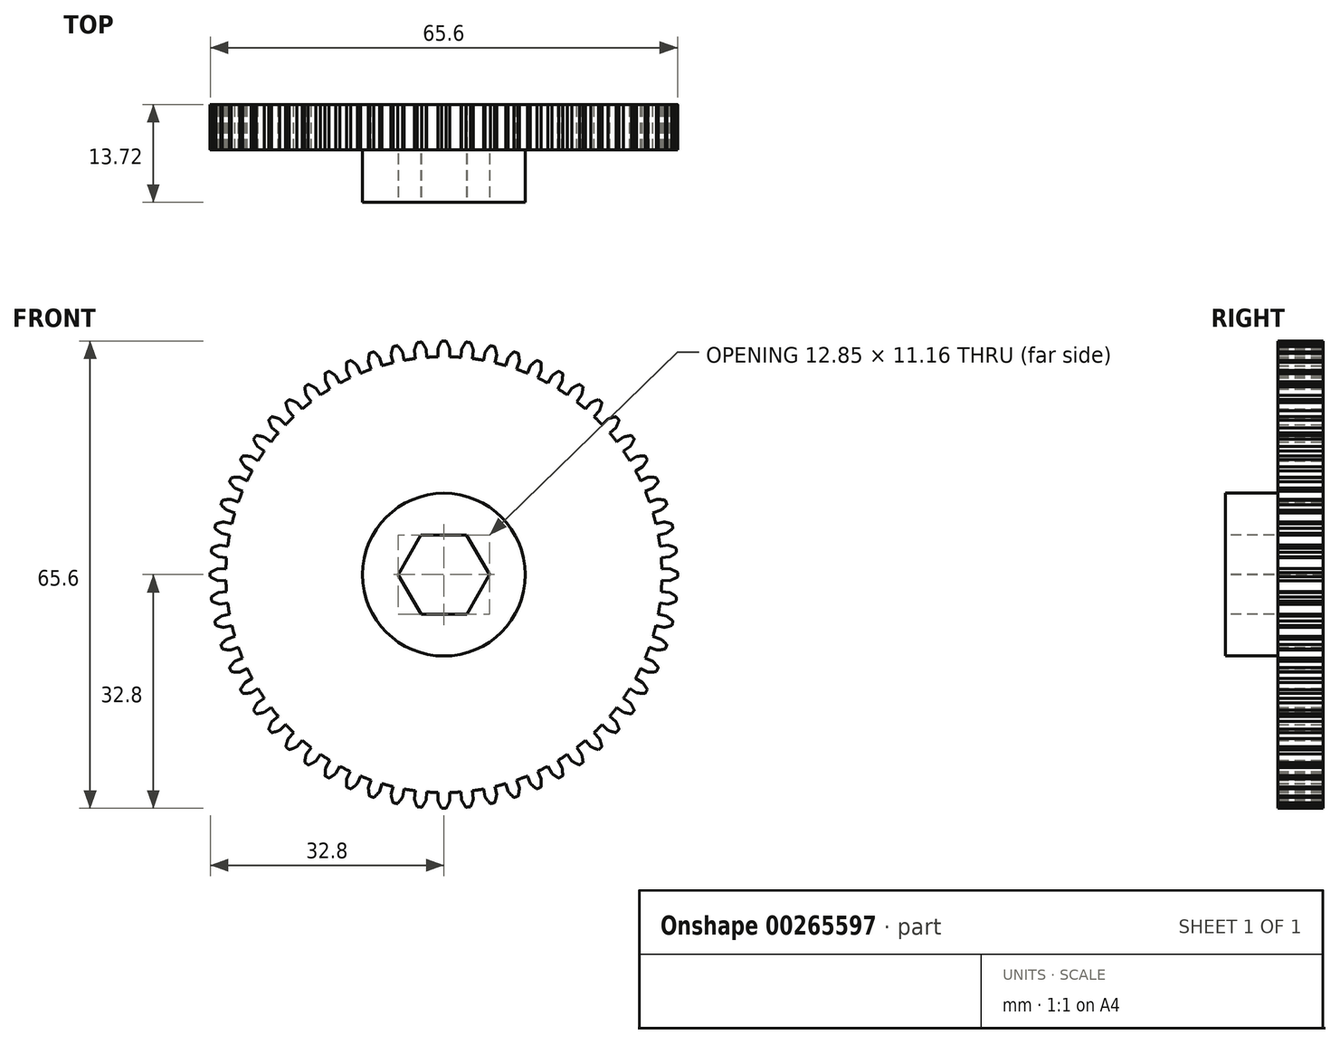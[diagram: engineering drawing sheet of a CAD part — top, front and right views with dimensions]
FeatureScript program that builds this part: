
annotation { "Feature Type Name" : "Feature", "Feature Type Description" : "" }
export const myFeature = defineFeature(function(context is Context, id is Id, definition is map)
    precondition{}
    {
        {
            var Q0;
            Q0=qCreatedBy(makeId("Front.planeOp"),FACE);
            var sketch = newSketch(context, id + "F0", { "sketchPlane" : qUnion([Q0])});
            skCircle(sketch, "E0", {"center": v(0, 0) * mm, "radius": 30.6 * mm});
            skArc(sketch, "E1", {"start": v(0.31, 32.8) * mm, "mid": v(0.16, 32.8) * mm, "end": v(0, 32.8) * mm});
            skLineSegment(sketch, "E2", {"start": v(0.8, 30.6) * mm, "end": v(0.83, 31.74) * mm});
            skLineSegment(sketch, "E3.trimOffspring", {"start": v(-1.66, 31.7) * mm, "end": v(-1.66, 31.74) * mm});
            skArc(sketch, "E4.trimOffspring", {"start": v(0.83, 31.74) * mm, "mid": v(0.6, 32.28) * mm, "end": v(0.31, 32.8) * mm});
            skLineSegment(sketch, "E5", {"start": v(0, 0) * mm, "end": v(0, 44.4) * mm, "construction": true});
            skArc(sketch, "E6.MirrorCS", {"start": v(-0.83, 31.74) * mm, "mid": v(-0.6, 32.28) * mm, "end": v(-0.31, 32.8) * mm});
            skPoint(sketch, "E7.orphan", {"position": v(-1.15, 44.01) * mm});
            skPoint(sketch, "E8.orphan", {"position": v(1.15, 44.01) * mm});
            skLineSegment(sketch, "E9.MirrorCS", {"start": v(-0.8, 30.6) * mm, "end": v(-0.83, 31.74) * mm});
            skArc(sketch, "E10.MirrorCS", {"start": v(-0.31, 32.8) * mm, "mid": v(-0.16, 32.8) * mm, "end": v(0, 32.8) * mm});
            skArc(sketch, "E11.1.0", {"start": v(-2.5, 31.65) * mm, "mid": v(-2.79, 32.17) * mm, "end": v(-3.12, 32.66) * mm});
            skLineSegment(sketch, "E11.1.1", {"start": v(-4, 30.35) * mm, "end": v(-4.14, 31.48) * mm});
            skLineSegment(sketch, "E11.1.2", {"start": v(-2.4, 30.51) * mm, "end": v(-2.5, 31.65) * mm});
            skArc(sketch, "E11.1.3", {"start": v(-4.14, 31.48) * mm, "mid": v(-3.96, 32.04) * mm, "end": v(-3.74, 32.6) * mm});
            skArc(sketch, "E11.1.4", {"start": v(-3.12, 32.66) * mm, "mid": v(-3.27, 32.64) * mm, "end": v(-3.43, 32.62) * mm});
            skArc(sketch, "E11.1.5", {"start": v(-3.74, 32.6) * mm, "mid": v(-3.58, 32.6) * mm, "end": v(-3.43, 32.62) * mm});
            skArc(sketch, "E11.2.0", {"start": v(-5.79, 31.22) * mm, "mid": v(-6.13, 31.7) * mm, "end": v(-6.51, 32.15) * mm});
            skLineSegment(sketch, "E11.2.1", {"start": v(-7.15, 29.76) * mm, "end": v(-7.41, 30.87) * mm});
            skLineSegment(sketch, "E11.2.2", {"start": v(-5.58, 30.1) * mm, "end": v(-5.79, 31.22) * mm});
            skArc(sketch, "E11.2.3", {"start": v(-7.41, 30.87) * mm, "mid": v(-7.3, 31.45) * mm, "end": v(-7.13, 32.02) * mm});
            skArc(sketch, "E11.2.4", {"start": v(-6.51, 32.15) * mm, "mid": v(-6.67, 32.12) * mm, "end": v(-6.82, 32.09) * mm});
            skArc(sketch, "E11.2.5", {"start": v(-7.13, 32.02) * mm, "mid": v(-6.97, 32.05) * mm, "end": v(-6.82, 32.09) * mm});
            skArc(sketch, "E11.3.0", {"start": v(-9.02, 30.44) * mm, "mid": v(-9.41, 30.88) * mm, "end": v(-9.84, 31.3) * mm});
            skLineSegment(sketch, "E11.3.1", {"start": v(-10.22, 28.85) * mm, "end": v(-10.6, 29.93) * mm});
            skLineSegment(sketch, "E11.3.2", {"start": v(-8.7, 29.35) * mm, "end": v(-9.02, 30.44) * mm});
            skArc(sketch, "E11.3.3", {"start": v(-10.6, 29.93) * mm, "mid": v(-10.54, 30.52) * mm, "end": v(-10.43, 31.1) * mm});
            skArc(sketch, "E11.3.4", {"start": v(-9.84, 31.3) * mm, "mid": v(-9.99, 31.25) * mm, "end": v(-10.14, 31.2) * mm});
            skArc(sketch, "E11.3.5", {"start": v(-10.43, 31.1) * mm, "mid": v(-10.29, 31.15) * mm, "end": v(-10.14, 31.2) * mm});
            skArc(sketch, "E11.4.0", {"start": v(-12.15, 29.33) * mm, "mid": v(-12.59, 29.73) * mm, "end": v(-13.06, 30.1) * mm});
            skLineSegment(sketch, "E11.4.1", {"start": v(-13.18, 27.63) * mm, "end": v(-13.67, 28.66) * mm});
            skLineSegment(sketch, "E11.4.2", {"start": v(-11.71, 28.28) * mm, "end": v(-12.15, 29.33) * mm});
            skArc(sketch, "E11.4.3", {"start": v(-13.67, 28.66) * mm, "mid": v(-13.67, 29.25) * mm, "end": v(-13.63, 29.84) * mm});
            skArc(sketch, "E11.4.4", {"start": v(-13.06, 30.1) * mm, "mid": v(-13.2, 30.03) * mm, "end": v(-13.34, 29.97) * mm});
            skArc(sketch, "E11.4.5", {"start": v(-13.63, 29.84) * mm, "mid": v(-13.49, 29.9) * mm, "end": v(-13.34, 29.97) * mm});
            skArc(sketch, "E11.5.0", {"start": v(-15.15, 27.9) * mm, "mid": v(-15.63, 28.25) * mm, "end": v(-16.13, 28.56) * mm});
            skLineSegment(sketch, "E11.5.1", {"start": v(-16, 26.1) * mm, "end": v(-16.59, 27.07) * mm});
            skLineSegment(sketch, "E11.5.2", {"start": v(-14.6, 26.9) * mm, "end": v(-15.15, 27.9) * mm});
            skArc(sketch, "E11.5.3", {"start": v(-16.59, 27.07) * mm, "mid": v(-16.65, 27.66) * mm, "end": v(-16.67, 28.25) * mm});
            skArc(sketch, "E11.5.4", {"start": v(-16.13, 28.56) * mm, "mid": v(-16.27, 28.49) * mm, "end": v(-16.4, 28.4) * mm});
            skArc(sketch, "E11.5.5", {"start": v(-16.67, 28.25) * mm, "mid": v(-16.54, 28.33) * mm, "end": v(-16.4, 28.4) * mm});
            skArc(sketch, "E11.6.0", {"start": v(-17.98, 26.17) * mm, "mid": v(-18.5, 26.46) * mm, "end": v(-19.03, 26.72) * mm});
            skLineSegment(sketch, "E11.6.1", {"start": v(-18.63, 24.28) * mm, "end": v(-19.33, 25.19) * mm});
            skLineSegment(sketch, "E11.6.2", {"start": v(-17.34, 25.22) * mm, "end": v(-17.98, 26.17) * mm});
            skArc(sketch, "E11.6.3", {"start": v(-19.33, 25.19) * mm, "mid": v(-19.45, 25.77) * mm, "end": v(-19.53, 26.35) * mm});
            skArc(sketch, "E11.6.4", {"start": v(-19.03, 26.72) * mm, "mid": v(-19.15, 26.63) * mm, "end": v(-19.28, 26.54) * mm});
            skArc(sketch, "E11.6.5", {"start": v(-19.53, 26.35) * mm, "mid": v(-19.4, 26.45) * mm, "end": v(-19.28, 26.54) * mm});
            skArc(sketch, "E11.7.0", {"start": v(-20.62, 24.14) * mm, "mid": v(-21.16, 24.39) * mm, "end": v(-21.72, 24.59) * mm});
            skLineSegment(sketch, "E11.7.1", {"start": v(-21.07, 22.2) * mm, "end": v(-21.86, 23.03) * mm});
            skLineSegment(sketch, "E11.7.2", {"start": v(-19.88, 23.27) * mm, "end": v(-20.62, 24.14) * mm});
            skArc(sketch, "E11.7.3", {"start": v(-21.86, 23.03) * mm, "mid": v(-22.04, 23.6) * mm, "end": v(-22.18, 24.17) * mm});
            skArc(sketch, "E11.7.4", {"start": v(-21.72, 24.59) * mm, "mid": v(-21.83, 24.48) * mm, "end": v(-21.95, 24.38) * mm});
            skArc(sketch, "E11.7.5", {"start": v(-22.18, 24.17) * mm, "mid": v(-22.07, 24.27) * mm, "end": v(-21.95, 24.38) * mm});
            skArc(sketch, "E11.8.0", {"start": v(-23.03, 21.86) * mm, "mid": v(-23.6, 22.04) * mm, "end": v(-24.17, 22.18) * mm});
            skLineSegment(sketch, "E11.8.1", {"start": v(-23.27, 19.88) * mm, "end": v(-24.14, 20.62) * mm});
            skLineSegment(sketch, "E11.8.2", {"start": v(-22.2, 21.07) * mm, "end": v(-23.03, 21.86) * mm});
            skArc(sketch, "E11.8.3", {"start": v(-24.14, 20.62) * mm, "mid": v(-24.39, 21.16) * mm, "end": v(-24.59, 21.72) * mm});
            skArc(sketch, "E11.8.4", {"start": v(-24.17, 22.18) * mm, "mid": v(-24.27, 22.07) * mm, "end": v(-24.38, 21.95) * mm});
            skArc(sketch, "E11.8.5", {"start": v(-24.59, 21.72) * mm, "mid": v(-24.48, 21.83) * mm, "end": v(-24.38, 21.95) * mm});
            skArc(sketch, "E11.9.0", {"start": v(-25.19, 19.33) * mm, "mid": v(-25.77, 19.45) * mm, "end": v(-26.35, 19.53) * mm});
            skLineSegment(sketch, "E11.9.1", {"start": v(-25.22, 17.34) * mm, "end": v(-26.17, 17.98) * mm});
            skLineSegment(sketch, "E11.9.2", {"start": v(-24.28, 18.63) * mm, "end": v(-25.19, 19.33) * mm});
            skArc(sketch, "E11.9.3", {"start": v(-26.17, 17.98) * mm, "mid": v(-26.46, 18.5) * mm, "end": v(-26.72, 19.03) * mm});
            skArc(sketch, "E11.9.4", {"start": v(-26.35, 19.53) * mm, "mid": v(-26.45, 19.4) * mm, "end": v(-26.54, 19.28) * mm});
            skArc(sketch, "E11.9.5", {"start": v(-26.72, 19.03) * mm, "mid": v(-26.63, 19.15) * mm, "end": v(-26.54, 19.28) * mm});
            skArc(sketch, "E11.10.0", {"start": v(-27.07, 16.59) * mm, "mid": v(-27.66, 16.65) * mm, "end": v(-28.25, 16.67) * mm});
            skLineSegment(sketch, "E11.10.1", {"start": v(-26.9, 14.6) * mm, "end": v(-27.9, 15.15) * mm});
            skLineSegment(sketch, "E11.10.2", {"start": v(-26.1, 16) * mm, "end": v(-27.07, 16.59) * mm});
            skArc(sketch, "E11.10.3", {"start": v(-27.9, 15.15) * mm, "mid": v(-28.25, 15.63) * mm, "end": v(-28.56, 16.13) * mm});
            skArc(sketch, "E11.10.4", {"start": v(-28.25, 16.67) * mm, "mid": v(-28.33, 16.54) * mm, "end": v(-28.4, 16.4) * mm});
            skArc(sketch, "E11.10.5", {"start": v(-28.56, 16.13) * mm, "mid": v(-28.49, 16.27) * mm, "end": v(-28.4, 16.4) * mm});
            skArc(sketch, "E11.11.0", {"start": v(-28.66, 13.67) * mm, "mid": v(-29.25, 13.67) * mm, "end": v(-29.84, 13.63) * mm});
            skLineSegment(sketch, "E11.11.1", {"start": v(-28.28, 11.71) * mm, "end": v(-29.33, 12.15) * mm});
            skLineSegment(sketch, "E11.11.2", {"start": v(-27.63, 13.18) * mm, "end": v(-28.66, 13.67) * mm});
            skArc(sketch, "E11.11.3", {"start": v(-29.33, 12.15) * mm, "mid": v(-29.73, 12.59) * mm, "end": v(-30.1, 13.06) * mm});
            skArc(sketch, "E11.11.4", {"start": v(-29.84, 13.63) * mm, "mid": v(-29.9, 13.49) * mm, "end": v(-29.97, 13.34) * mm});
            skArc(sketch, "E11.11.5", {"start": v(-30.1, 13.06) * mm, "mid": v(-30.03, 13.2) * mm, "end": v(-29.97, 13.34) * mm});
            skArc(sketch, "E11.12.0", {"start": v(-29.93, 10.6) * mm, "mid": v(-30.52, 10.54) * mm, "end": v(-31.1, 10.43) * mm});
            skLineSegment(sketch, "E11.12.1", {"start": v(-29.35, 8.7) * mm, "end": v(-30.44, 9.02) * mm});
            skLineSegment(sketch, "E11.12.2", {"start": v(-28.85, 10.22) * mm, "end": v(-29.93, 10.6) * mm});
            skArc(sketch, "E11.12.3", {"start": v(-30.44, 9.02) * mm, "mid": v(-30.88, 9.41) * mm, "end": v(-31.3, 9.84) * mm});
            skArc(sketch, "E11.12.4", {"start": v(-31.1, 10.43) * mm, "mid": v(-31.15, 10.29) * mm, "end": v(-31.2, 10.14) * mm});
            skArc(sketch, "E11.12.5", {"start": v(-31.3, 9.84) * mm, "mid": v(-31.25, 9.99) * mm, "end": v(-31.2, 10.14) * mm});
            skArc(sketch, "E11.13.0", {"start": v(-30.87, 7.41) * mm, "mid": v(-31.45, 7.3) * mm, "end": v(-32.02, 7.13) * mm});
            skLineSegment(sketch, "E11.13.1", {"start": v(-30.1, 5.58) * mm, "end": v(-31.22, 5.79) * mm});
            skLineSegment(sketch, "E11.13.2", {"start": v(-29.76, 7.15) * mm, "end": v(-30.87, 7.41) * mm});
            skArc(sketch, "E11.13.3", {"start": v(-31.22, 5.79) * mm, "mid": v(-31.7, 6.13) * mm, "end": v(-32.15, 6.51) * mm});
            skArc(sketch, "E11.13.4", {"start": v(-32.02, 7.13) * mm, "mid": v(-32.05, 6.97) * mm, "end": v(-32.09, 6.82) * mm});
            skArc(sketch, "E11.13.5", {"start": v(-32.15, 6.51) * mm, "mid": v(-32.12, 6.67) * mm, "end": v(-32.09, 6.82) * mm});
            skArc(sketch, "E11.14.0", {"start": v(-31.48, 4.14) * mm, "mid": v(-32.04, 3.96) * mm, "end": v(-32.6, 3.74) * mm});
            skLineSegment(sketch, "E11.14.1", {"start": v(-30.51, 2.4) * mm, "end": v(-31.65, 2.5) * mm});
            skLineSegment(sketch, "E11.14.2", {"start": v(-30.35, 4) * mm, "end": v(-31.48, 4.14) * mm});
            skArc(sketch, "E11.14.3", {"start": v(-31.65, 2.5) * mm, "mid": v(-32.17, 2.79) * mm, "end": v(-32.66, 3.12) * mm});
            skArc(sketch, "E11.14.4", {"start": v(-32.6, 3.74) * mm, "mid": v(-32.6, 3.58) * mm, "end": v(-32.62, 3.43) * mm});
            skArc(sketch, "E11.14.5", {"start": v(-32.66, 3.12) * mm, "mid": v(-32.64, 3.27) * mm, "end": v(-32.62, 3.43) * mm});
            skArc(sketch, "E11.15.0", {"start": v(-31.74, 0.83) * mm, "mid": v(-32.28, 0.6) * mm, "end": v(-32.8, 0.31) * mm});
            skLineSegment(sketch, "E11.15.1", {"start": v(-30.6, -0.8) * mm, "end": v(-31.74, -0.83) * mm});
            skLineSegment(sketch, "E11.15.2", {"start": v(-30.6, 0.8) * mm, "end": v(-31.74, 0.83) * mm});
            skArc(sketch, "E11.15.3", {"start": v(-31.74, -0.83) * mm, "mid": v(-32.28, -0.6) * mm, "end": v(-32.8, -0.31) * mm});
            skArc(sketch, "E11.15.4", {"start": v(-32.8, 0.31) * mm, "mid": v(-32.8, 0.16) * mm, "end": v(-32.8, 0) * mm});
            skArc(sketch, "E11.15.5", {"start": v(-32.8, -0.31) * mm, "mid": v(-32.8, -0.16) * mm, "end": v(-32.8, 0) * mm});
            skArc(sketch, "E11.16.0", {"start": v(-31.65, -2.5) * mm, "mid": v(-32.17, -2.79) * mm, "end": v(-32.66, -3.12) * mm});
            skLineSegment(sketch, "E11.16.1", {"start": v(-30.35, -4) * mm, "end": v(-31.48, -4.14) * mm});
            skLineSegment(sketch, "E11.16.2", {"start": v(-30.51, -2.4) * mm, "end": v(-31.65, -2.5) * mm});
            skArc(sketch, "E11.16.3", {"start": v(-31.48, -4.14) * mm, "mid": v(-32.04, -3.96) * mm, "end": v(-32.6, -3.74) * mm});
            skArc(sketch, "E11.16.4", {"start": v(-32.66, -3.12) * mm, "mid": v(-32.64, -3.27) * mm, "end": v(-32.62, -3.43) * mm});
            skArc(sketch, "E11.16.5", {"start": v(-32.6, -3.74) * mm, "mid": v(-32.6, -3.58) * mm, "end": v(-32.62, -3.43) * mm});
            skArc(sketch, "E11.17.0", {"start": v(-31.22, -5.79) * mm, "mid": v(-31.7, -6.13) * mm, "end": v(-32.15, -6.51) * mm});
            skLineSegment(sketch, "E11.17.1", {"start": v(-29.76, -7.15) * mm, "end": v(-30.87, -7.41) * mm});
            skLineSegment(sketch, "E11.17.2", {"start": v(-30.1, -5.58) * mm, "end": v(-31.22, -5.79) * mm});
            skArc(sketch, "E11.17.3", {"start": v(-30.87, -7.41) * mm, "mid": v(-31.45, -7.3) * mm, "end": v(-32.02, -7.13) * mm});
            skArc(sketch, "E11.17.4", {"start": v(-32.15, -6.51) * mm, "mid": v(-32.12, -6.67) * mm, "end": v(-32.09, -6.82) * mm});
            skArc(sketch, "E11.17.5", {"start": v(-32.02, -7.13) * mm, "mid": v(-32.05, -6.97) * mm, "end": v(-32.09, -6.82) * mm});
            skArc(sketch, "E11.18.0", {"start": v(-30.44, -9.02) * mm, "mid": v(-30.88, -9.41) * mm, "end": v(-31.3, -9.84) * mm});
            skLineSegment(sketch, "E11.18.1", {"start": v(-28.85, -10.22) * mm, "end": v(-29.93, -10.6) * mm});
            skLineSegment(sketch, "E11.18.2", {"start": v(-29.35, -8.7) * mm, "end": v(-30.44, -9.02) * mm});
            skArc(sketch, "E11.18.3", {"start": v(-29.93, -10.6) * mm, "mid": v(-30.52, -10.54) * mm, "end": v(-31.1, -10.43) * mm});
            skArc(sketch, "E11.18.4", {"start": v(-31.3, -9.84) * mm, "mid": v(-31.25, -9.99) * mm, "end": v(-31.2, -10.14) * mm});
            skArc(sketch, "E11.18.5", {"start": v(-31.1, -10.43) * mm, "mid": v(-31.15, -10.29) * mm, "end": v(-31.2, -10.14) * mm});
            skArc(sketch, "E11.19.0", {"start": v(-29.33, -12.15) * mm, "mid": v(-29.73, -12.59) * mm, "end": v(-30.1, -13.06) * mm});
            skLineSegment(sketch, "E11.19.1", {"start": v(-27.63, -13.18) * mm, "end": v(-28.66, -13.67) * mm});
            skLineSegment(sketch, "E11.19.2", {"start": v(-28.28, -11.71) * mm, "end": v(-29.33, -12.15) * mm});
            skArc(sketch, "E11.19.3", {"start": v(-28.66, -13.67) * mm, "mid": v(-29.25, -13.67) * mm, "end": v(-29.84, -13.63) * mm});
            skArc(sketch, "E11.19.4", {"start": v(-30.1, -13.06) * mm, "mid": v(-30.03, -13.2) * mm, "end": v(-29.97, -13.34) * mm});
            skArc(sketch, "E11.19.5", {"start": v(-29.84, -13.63) * mm, "mid": v(-29.9, -13.49) * mm, "end": v(-29.97, -13.34) * mm});
            skArc(sketch, "E11.20.0", {"start": v(-27.9, -15.15) * mm, "mid": v(-28.25, -15.63) * mm, "end": v(-28.56, -16.13) * mm});
            skLineSegment(sketch, "E11.20.1", {"start": v(-26.1, -16) * mm, "end": v(-27.07, -16.59) * mm});
            skLineSegment(sketch, "E11.20.2", {"start": v(-26.9, -14.6) * mm, "end": v(-27.9, -15.15) * mm});
            skArc(sketch, "E11.20.3", {"start": v(-27.07, -16.59) * mm, "mid": v(-27.66, -16.65) * mm, "end": v(-28.25, -16.67) * mm});
            skArc(sketch, "E11.20.4", {"start": v(-28.56, -16.13) * mm, "mid": v(-28.49, -16.27) * mm, "end": v(-28.4, -16.4) * mm});
            skArc(sketch, "E11.20.5", {"start": v(-28.25, -16.67) * mm, "mid": v(-28.33, -16.54) * mm, "end": v(-28.4, -16.4) * mm});
            skArc(sketch, "E11.21.0", {"start": v(-26.17, -17.98) * mm, "mid": v(-26.46, -18.5) * mm, "end": v(-26.72, -19.03) * mm});
            skLineSegment(sketch, "E11.21.1", {"start": v(-24.28, -18.63) * mm, "end": v(-25.19, -19.33) * mm});
            skLineSegment(sketch, "E11.21.2", {"start": v(-25.22, -17.34) * mm, "end": v(-26.17, -17.98) * mm});
            skArc(sketch, "E11.21.3", {"start": v(-25.19, -19.33) * mm, "mid": v(-25.77, -19.45) * mm, "end": v(-26.35, -19.53) * mm});
            skArc(sketch, "E11.21.4", {"start": v(-26.72, -19.03) * mm, "mid": v(-26.63, -19.15) * mm, "end": v(-26.54, -19.28) * mm});
            skArc(sketch, "E11.21.5", {"start": v(-26.35, -19.53) * mm, "mid": v(-26.45, -19.4) * mm, "end": v(-26.54, -19.28) * mm});
            skArc(sketch, "E11.22.0", {"start": v(-24.14, -20.62) * mm, "mid": v(-24.39, -21.16) * mm, "end": v(-24.59, -21.72) * mm});
            skLineSegment(sketch, "E11.22.1", {"start": v(-22.2, -21.07) * mm, "end": v(-23.03, -21.86) * mm});
            skLineSegment(sketch, "E11.22.2", {"start": v(-23.27, -19.88) * mm, "end": v(-24.14, -20.62) * mm});
            skArc(sketch, "E11.22.3", {"start": v(-23.03, -21.86) * mm, "mid": v(-23.6, -22.04) * mm, "end": v(-24.17, -22.18) * mm});
            skArc(sketch, "E11.22.4", {"start": v(-24.59, -21.72) * mm, "mid": v(-24.48, -21.83) * mm, "end": v(-24.38, -21.95) * mm});
            skArc(sketch, "E11.22.5", {"start": v(-24.17, -22.18) * mm, "mid": v(-24.27, -22.07) * mm, "end": v(-24.38, -21.95) * mm});
            skArc(sketch, "E11.23.0", {"start": v(-21.86, -23.03) * mm, "mid": v(-22.04, -23.6) * mm, "end": v(-22.18, -24.17) * mm});
            skLineSegment(sketch, "E11.23.1", {"start": v(-19.88, -23.27) * mm, "end": v(-20.62, -24.14) * mm});
            skLineSegment(sketch, "E11.23.2", {"start": v(-21.07, -22.2) * mm, "end": v(-21.86, -23.03) * mm});
            skArc(sketch, "E11.23.3", {"start": v(-20.62, -24.14) * mm, "mid": v(-21.16, -24.39) * mm, "end": v(-21.72, -24.59) * mm});
            skArc(sketch, "E11.23.4", {"start": v(-22.18, -24.17) * mm, "mid": v(-22.07, -24.27) * mm, "end": v(-21.95, -24.38) * mm});
            skArc(sketch, "E11.23.5", {"start": v(-21.72, -24.59) * mm, "mid": v(-21.83, -24.48) * mm, "end": v(-21.95, -24.38) * mm});
            skArc(sketch, "E11.24.0", {"start": v(-19.33, -25.19) * mm, "mid": v(-19.45, -25.77) * mm, "end": v(-19.53, -26.35) * mm});
            skLineSegment(sketch, "E11.24.1", {"start": v(-17.34, -25.22) * mm, "end": v(-17.98, -26.17) * mm});
            skLineSegment(sketch, "E11.24.2", {"start": v(-18.63, -24.28) * mm, "end": v(-19.33, -25.19) * mm});
            skArc(sketch, "E11.24.3", {"start": v(-17.98, -26.17) * mm, "mid": v(-18.5, -26.46) * mm, "end": v(-19.03, -26.72) * mm});
            skArc(sketch, "E11.24.4", {"start": v(-19.53, -26.35) * mm, "mid": v(-19.4, -26.45) * mm, "end": v(-19.28, -26.54) * mm});
            skArc(sketch, "E11.24.5", {"start": v(-19.03, -26.72) * mm, "mid": v(-19.15, -26.63) * mm, "end": v(-19.28, -26.54) * mm});
            skArc(sketch, "E11.25.0", {"start": v(-16.59, -27.07) * mm, "mid": v(-16.65, -27.66) * mm, "end": v(-16.67, -28.25) * mm});
            skLineSegment(sketch, "E11.25.1", {"start": v(-14.6, -26.9) * mm, "end": v(-15.15, -27.9) * mm});
            skLineSegment(sketch, "E11.25.2", {"start": v(-16, -26.1) * mm, "end": v(-16.59, -27.07) * mm});
            skArc(sketch, "E11.25.3", {"start": v(-15.15, -27.9) * mm, "mid": v(-15.63, -28.25) * mm, "end": v(-16.13, -28.56) * mm});
            skArc(sketch, "E11.25.4", {"start": v(-16.67, -28.25) * mm, "mid": v(-16.54, -28.33) * mm, "end": v(-16.4, -28.4) * mm});
            skArc(sketch, "E11.25.5", {"start": v(-16.13, -28.56) * mm, "mid": v(-16.27, -28.49) * mm, "end": v(-16.4, -28.4) * mm});
            skArc(sketch, "E11.26.0", {"start": v(-13.67, -28.66) * mm, "mid": v(-13.67, -29.25) * mm, "end": v(-13.63, -29.84) * mm});
            skLineSegment(sketch, "E11.26.1", {"start": v(-11.71, -28.28) * mm, "end": v(-12.15, -29.33) * mm});
            skLineSegment(sketch, "E11.26.2", {"start": v(-13.18, -27.63) * mm, "end": v(-13.67, -28.66) * mm});
            skArc(sketch, "E11.26.3", {"start": v(-12.15, -29.33) * mm, "mid": v(-12.59, -29.73) * mm, "end": v(-13.06, -30.1) * mm});
            skArc(sketch, "E11.26.4", {"start": v(-13.63, -29.84) * mm, "mid": v(-13.49, -29.9) * mm, "end": v(-13.34, -29.97) * mm});
            skArc(sketch, "E11.26.5", {"start": v(-13.06, -30.1) * mm, "mid": v(-13.2, -30.03) * mm, "end": v(-13.34, -29.97) * mm});
            skArc(sketch, "E11.27.0", {"start": v(-10.6, -29.93) * mm, "mid": v(-10.54, -30.52) * mm, "end": v(-10.43, -31.1) * mm});
            skLineSegment(sketch, "E11.27.1", {"start": v(-8.7, -29.35) * mm, "end": v(-9.02, -30.44) * mm});
            skLineSegment(sketch, "E11.27.2", {"start": v(-10.22, -28.85) * mm, "end": v(-10.6, -29.93) * mm});
            skArc(sketch, "E11.27.3", {"start": v(-9.02, -30.44) * mm, "mid": v(-9.41, -30.88) * mm, "end": v(-9.84, -31.3) * mm});
            skArc(sketch, "E11.27.4", {"start": v(-10.43, -31.1) * mm, "mid": v(-10.29, -31.15) * mm, "end": v(-10.14, -31.2) * mm});
            skArc(sketch, "E11.27.5", {"start": v(-9.84, -31.3) * mm, "mid": v(-9.99, -31.25) * mm, "end": v(-10.14, -31.2) * mm});
            skArc(sketch, "E11.28.0", {"start": v(-7.41, -30.87) * mm, "mid": v(-7.3, -31.45) * mm, "end": v(-7.13, -32.02) * mm});
            skLineSegment(sketch, "E11.28.1", {"start": v(-5.58, -30.1) * mm, "end": v(-5.79, -31.22) * mm});
            skLineSegment(sketch, "E11.28.2", {"start": v(-7.15, -29.76) * mm, "end": v(-7.41, -30.87) * mm});
            skArc(sketch, "E11.28.3", {"start": v(-5.79, -31.22) * mm, "mid": v(-6.13, -31.7) * mm, "end": v(-6.51, -32.15) * mm});
            skArc(sketch, "E11.28.4", {"start": v(-7.13, -32.02) * mm, "mid": v(-6.97, -32.05) * mm, "end": v(-6.82, -32.09) * mm});
            skArc(sketch, "E11.28.5", {"start": v(-6.51, -32.15) * mm, "mid": v(-6.67, -32.12) * mm, "end": v(-6.82, -32.09) * mm});
            skArc(sketch, "E11.29.0", {"start": v(-4.14, -31.48) * mm, "mid": v(-3.96, -32.04) * mm, "end": v(-3.74, -32.6) * mm});
            skLineSegment(sketch, "E11.29.1", {"start": v(-2.4, -30.51) * mm, "end": v(-2.5, -31.65) * mm});
            skLineSegment(sketch, "E11.29.2", {"start": v(-4, -30.35) * mm, "end": v(-4.14, -31.48) * mm});
            skArc(sketch, "E11.29.3", {"start": v(-2.5, -31.65) * mm, "mid": v(-2.79, -32.17) * mm, "end": v(-3.12, -32.66) * mm});
            skArc(sketch, "E11.29.4", {"start": v(-3.74, -32.6) * mm, "mid": v(-3.58, -32.6) * mm, "end": v(-3.43, -32.62) * mm});
            skArc(sketch, "E11.29.5", {"start": v(-3.12, -32.66) * mm, "mid": v(-3.27, -32.64) * mm, "end": v(-3.43, -32.62) * mm});
            skArc(sketch, "E11.30.0", {"start": v(-0.83, -31.74) * mm, "mid": v(-0.6, -32.28) * mm, "end": v(-0.31, -32.8) * mm});
            skLineSegment(sketch, "E11.30.1", {"start": v(0.8, -30.6) * mm, "end": v(0.83, -31.74) * mm});
            skLineSegment(sketch, "E11.30.2", {"start": v(-0.8, -30.6) * mm, "end": v(-0.83, -31.74) * mm});
            skArc(sketch, "E11.30.3", {"start": v(0.83, -31.74) * mm, "mid": v(0.6, -32.28) * mm, "end": v(0.31, -32.8) * mm});
            skArc(sketch, "E11.30.4", {"start": v(-0.31, -32.8) * mm, "mid": v(-0.16, -32.8) * mm, "end": v(0, -32.8) * mm});
            skArc(sketch, "E11.30.5", {"start": v(0.31, -32.8) * mm, "mid": v(0.16, -32.8) * mm, "end": v(0, -32.8) * mm});
            skArc(sketch, "E11.31.0", {"start": v(2.5, -31.65) * mm, "mid": v(2.79, -32.17) * mm, "end": v(3.12, -32.66) * mm});
            skLineSegment(sketch, "E11.31.1", {"start": v(4, -30.35) * mm, "end": v(4.14, -31.48) * mm});
            skLineSegment(sketch, "E11.31.2", {"start": v(2.4, -30.51) * mm, "end": v(2.5, -31.65) * mm});
            skArc(sketch, "E11.31.3", {"start": v(4.14, -31.48) * mm, "mid": v(3.96, -32.04) * mm, "end": v(3.74, -32.6) * mm});
            skArc(sketch, "E11.31.4", {"start": v(3.12, -32.66) * mm, "mid": v(3.27, -32.64) * mm, "end": v(3.43, -32.62) * mm});
            skArc(sketch, "E11.31.5", {"start": v(3.74, -32.6) * mm, "mid": v(3.58, -32.6) * mm, "end": v(3.43, -32.62) * mm});
            skArc(sketch, "E11.32.0", {"start": v(5.79, -31.22) * mm, "mid": v(6.13, -31.7) * mm, "end": v(6.51, -32.15) * mm});
            skLineSegment(sketch, "E11.32.1", {"start": v(7.15, -29.76) * mm, "end": v(7.41, -30.87) * mm});
            skLineSegment(sketch, "E11.32.2", {"start": v(5.58, -30.1) * mm, "end": v(5.79, -31.22) * mm});
            skArc(sketch, "E11.32.3", {"start": v(7.41, -30.87) * mm, "mid": v(7.3, -31.45) * mm, "end": v(7.13, -32.02) * mm});
            skArc(sketch, "E11.32.4", {"start": v(6.51, -32.15) * mm, "mid": v(6.67, -32.12) * mm, "end": v(6.82, -32.09) * mm});
            skArc(sketch, "E11.32.5", {"start": v(7.13, -32.02) * mm, "mid": v(6.97, -32.05) * mm, "end": v(6.82, -32.09) * mm});
            skArc(sketch, "E11.33.0", {"start": v(9.02, -30.44) * mm, "mid": v(9.41, -30.88) * mm, "end": v(9.84, -31.3) * mm});
            skLineSegment(sketch, "E11.33.1", {"start": v(10.22, -28.85) * mm, "end": v(10.6, -29.93) * mm});
            skLineSegment(sketch, "E11.33.2", {"start": v(8.7, -29.35) * mm, "end": v(9.02, -30.44) * mm});
            skArc(sketch, "E11.33.3", {"start": v(10.6, -29.93) * mm, "mid": v(10.54, -30.52) * mm, "end": v(10.43, -31.1) * mm});
            skArc(sketch, "E11.33.4", {"start": v(9.84, -31.3) * mm, "mid": v(9.99, -31.25) * mm, "end": v(10.14, -31.2) * mm});
            skArc(sketch, "E11.33.5", {"start": v(10.43, -31.1) * mm, "mid": v(10.29, -31.15) * mm, "end": v(10.14, -31.2) * mm});
            skArc(sketch, "E11.34.0", {"start": v(12.15, -29.33) * mm, "mid": v(12.59, -29.73) * mm, "end": v(13.06, -30.1) * mm});
            skLineSegment(sketch, "E11.34.1", {"start": v(13.18, -27.63) * mm, "end": v(13.67, -28.66) * mm});
            skLineSegment(sketch, "E11.34.2", {"start": v(11.71, -28.28) * mm, "end": v(12.15, -29.33) * mm});
            skArc(sketch, "E11.34.3", {"start": v(13.67, -28.66) * mm, "mid": v(13.67, -29.25) * mm, "end": v(13.63, -29.84) * mm});
            skArc(sketch, "E11.34.4", {"start": v(13.06, -30.1) * mm, "mid": v(13.2, -30.03) * mm, "end": v(13.34, -29.97) * mm});
            skArc(sketch, "E11.34.5", {"start": v(13.63, -29.84) * mm, "mid": v(13.49, -29.9) * mm, "end": v(13.34, -29.97) * mm});
            skArc(sketch, "E11.35.0", {"start": v(15.15, -27.9) * mm, "mid": v(15.63, -28.25) * mm, "end": v(16.13, -28.56) * mm});
            skLineSegment(sketch, "E11.35.1", {"start": v(16, -26.1) * mm, "end": v(16.59, -27.07) * mm});
            skLineSegment(sketch, "E11.35.2", {"start": v(14.6, -26.9) * mm, "end": v(15.15, -27.9) * mm});
            skArc(sketch, "E11.35.3", {"start": v(16.59, -27.07) * mm, "mid": v(16.65, -27.66) * mm, "end": v(16.67, -28.25) * mm});
            skArc(sketch, "E11.35.4", {"start": v(16.13, -28.56) * mm, "mid": v(16.27, -28.49) * mm, "end": v(16.4, -28.4) * mm});
            skArc(sketch, "E11.35.5", {"start": v(16.67, -28.25) * mm, "mid": v(16.54, -28.33) * mm, "end": v(16.4, -28.4) * mm});
            skArc(sketch, "E11.36.0", {"start": v(17.98, -26.17) * mm, "mid": v(18.5, -26.46) * mm, "end": v(19.03, -26.72) * mm});
            skLineSegment(sketch, "E11.36.1", {"start": v(18.63, -24.28) * mm, "end": v(19.33, -25.19) * mm});
            skLineSegment(sketch, "E11.36.2", {"start": v(17.34, -25.22) * mm, "end": v(17.98, -26.17) * mm});
            skArc(sketch, "E11.36.3", {"start": v(19.33, -25.19) * mm, "mid": v(19.45, -25.77) * mm, "end": v(19.53, -26.35) * mm});
            skArc(sketch, "E11.36.4", {"start": v(19.03, -26.72) * mm, "mid": v(19.15, -26.63) * mm, "end": v(19.28, -26.54) * mm});
            skArc(sketch, "E11.36.5", {"start": v(19.53, -26.35) * mm, "mid": v(19.4, -26.45) * mm, "end": v(19.28, -26.54) * mm});
            skArc(sketch, "E11.37.0", {"start": v(20.62, -24.14) * mm, "mid": v(21.16, -24.39) * mm, "end": v(21.72, -24.59) * mm});
            skLineSegment(sketch, "E11.37.1", {"start": v(21.07, -22.2) * mm, "end": v(21.86, -23.03) * mm});
            skLineSegment(sketch, "E11.37.2", {"start": v(19.88, -23.27) * mm, "end": v(20.62, -24.14) * mm});
            skArc(sketch, "E11.37.3", {"start": v(21.86, -23.03) * mm, "mid": v(22.04, -23.6) * mm, "end": v(22.18, -24.17) * mm});
            skArc(sketch, "E11.37.4", {"start": v(21.72, -24.59) * mm, "mid": v(21.83, -24.48) * mm, "end": v(21.95, -24.38) * mm});
            skArc(sketch, "E11.37.5", {"start": v(22.18, -24.17) * mm, "mid": v(22.07, -24.27) * mm, "end": v(21.95, -24.38) * mm});
            skArc(sketch, "E11.38.0", {"start": v(23.03, -21.86) * mm, "mid": v(23.6, -22.04) * mm, "end": v(24.17, -22.18) * mm});
            skLineSegment(sketch, "E11.38.1", {"start": v(23.27, -19.88) * mm, "end": v(24.14, -20.62) * mm});
            skLineSegment(sketch, "E11.38.2", {"start": v(22.2, -21.07) * mm, "end": v(23.03, -21.86) * mm});
            skArc(sketch, "E11.38.3", {"start": v(24.14, -20.62) * mm, "mid": v(24.39, -21.16) * mm, "end": v(24.59, -21.72) * mm});
            skArc(sketch, "E11.38.4", {"start": v(24.17, -22.18) * mm, "mid": v(24.27, -22.07) * mm, "end": v(24.38, -21.95) * mm});
            skArc(sketch, "E11.38.5", {"start": v(24.59, -21.72) * mm, "mid": v(24.48, -21.83) * mm, "end": v(24.38, -21.95) * mm});
            skArc(sketch, "E11.39.0", {"start": v(25.19, -19.33) * mm, "mid": v(25.77, -19.45) * mm, "end": v(26.35, -19.53) * mm});
            skLineSegment(sketch, "E11.39.1", {"start": v(25.22, -17.34) * mm, "end": v(26.17, -17.98) * mm});
            skLineSegment(sketch, "E11.39.2", {"start": v(24.28, -18.63) * mm, "end": v(25.19, -19.33) * mm});
            skArc(sketch, "E11.39.3", {"start": v(26.17, -17.98) * mm, "mid": v(26.46, -18.5) * mm, "end": v(26.72, -19.03) * mm});
            skArc(sketch, "E11.39.4", {"start": v(26.35, -19.53) * mm, "mid": v(26.45, -19.4) * mm, "end": v(26.54, -19.28) * mm});
            skArc(sketch, "E11.39.5", {"start": v(26.72, -19.03) * mm, "mid": v(26.63, -19.15) * mm, "end": v(26.54, -19.28) * mm});
            skArc(sketch, "E11.40.0", {"start": v(27.07, -16.59) * mm, "mid": v(27.66, -16.65) * mm, "end": v(28.25, -16.67) * mm});
            skLineSegment(sketch, "E11.40.1", {"start": v(26.9, -14.6) * mm, "end": v(27.9, -15.15) * mm});
            skLineSegment(sketch, "E11.40.2", {"start": v(26.1, -16) * mm, "end": v(27.07, -16.59) * mm});
            skArc(sketch, "E11.40.3", {"start": v(27.9, -15.15) * mm, "mid": v(28.25, -15.63) * mm, "end": v(28.56, -16.13) * mm});
            skArc(sketch, "E11.40.4", {"start": v(28.25, -16.67) * mm, "mid": v(28.33, -16.54) * mm, "end": v(28.4, -16.4) * mm});
            skArc(sketch, "E11.40.5", {"start": v(28.56, -16.13) * mm, "mid": v(28.49, -16.27) * mm, "end": v(28.4, -16.4) * mm});
            skArc(sketch, "E11.41.0", {"start": v(28.66, -13.67) * mm, "mid": v(29.25, -13.67) * mm, "end": v(29.84, -13.63) * mm});
            skLineSegment(sketch, "E11.41.1", {"start": v(28.28, -11.71) * mm, "end": v(29.33, -12.15) * mm});
            skLineSegment(sketch, "E11.41.2", {"start": v(27.63, -13.18) * mm, "end": v(28.66, -13.67) * mm});
            skArc(sketch, "E11.41.3", {"start": v(29.33, -12.15) * mm, "mid": v(29.73, -12.59) * mm, "end": v(30.1, -13.06) * mm});
            skArc(sketch, "E11.41.4", {"start": v(29.84, -13.63) * mm, "mid": v(29.9, -13.49) * mm, "end": v(29.97, -13.34) * mm});
            skArc(sketch, "E11.41.5", {"start": v(30.1, -13.06) * mm, "mid": v(30.03, -13.2) * mm, "end": v(29.97, -13.34) * mm});
            skArc(sketch, "E11.42.0", {"start": v(29.93, -10.6) * mm, "mid": v(30.52, -10.54) * mm, "end": v(31.1, -10.43) * mm});
            skLineSegment(sketch, "E11.42.1", {"start": v(29.35, -8.7) * mm, "end": v(30.44, -9.02) * mm});
            skLineSegment(sketch, "E11.42.2", {"start": v(28.85, -10.22) * mm, "end": v(29.93, -10.6) * mm});
            skArc(sketch, "E11.42.3", {"start": v(30.44, -9.02) * mm, "mid": v(30.88, -9.41) * mm, "end": v(31.3, -9.84) * mm});
            skArc(sketch, "E11.42.4", {"start": v(31.1, -10.43) * mm, "mid": v(31.15, -10.29) * mm, "end": v(31.2, -10.14) * mm});
            skArc(sketch, "E11.42.5", {"start": v(31.3, -9.84) * mm, "mid": v(31.25, -9.99) * mm, "end": v(31.2, -10.14) * mm});
            skArc(sketch, "E11.43.0", {"start": v(30.87, -7.41) * mm, "mid": v(31.45, -7.3) * mm, "end": v(32.02, -7.13) * mm});
            skLineSegment(sketch, "E11.43.1", {"start": v(30.1, -5.58) * mm, "end": v(31.22, -5.79) * mm});
            skLineSegment(sketch, "E11.43.2", {"start": v(29.76, -7.15) * mm, "end": v(30.87, -7.41) * mm});
            skArc(sketch, "E11.43.3", {"start": v(31.22, -5.79) * mm, "mid": v(31.7, -6.13) * mm, "end": v(32.15, -6.51) * mm});
            skArc(sketch, "E11.43.4", {"start": v(32.02, -7.13) * mm, "mid": v(32.05, -6.97) * mm, "end": v(32.09, -6.82) * mm});
            skArc(sketch, "E11.43.5", {"start": v(32.15, -6.51) * mm, "mid": v(32.12, -6.67) * mm, "end": v(32.09, -6.82) * mm});
            skArc(sketch, "E11.44.0", {"start": v(31.48, -4.14) * mm, "mid": v(32.04, -3.96) * mm, "end": v(32.6, -3.74) * mm});
            skLineSegment(sketch, "E11.44.1", {"start": v(30.51, -2.4) * mm, "end": v(31.65, -2.5) * mm});
            skLineSegment(sketch, "E11.44.2", {"start": v(30.35, -4) * mm, "end": v(31.48, -4.14) * mm});
            skArc(sketch, "E11.44.3", {"start": v(31.65, -2.5) * mm, "mid": v(32.17, -2.79) * mm, "end": v(32.66, -3.12) * mm});
            skArc(sketch, "E11.44.4", {"start": v(32.6, -3.74) * mm, "mid": v(32.6, -3.58) * mm, "end": v(32.62, -3.43) * mm});
            skArc(sketch, "E11.44.5", {"start": v(32.66, -3.12) * mm, "mid": v(32.64, -3.27) * mm, "end": v(32.62, -3.43) * mm});
            skArc(sketch, "E11.45.0", {"start": v(31.74, -0.83) * mm, "mid": v(32.28, -0.6) * mm, "end": v(32.8, -0.31) * mm});
            skLineSegment(sketch, "E11.45.1", {"start": v(30.6, 0.8) * mm, "end": v(31.74, 0.83) * mm});
            skLineSegment(sketch, "E11.45.2", {"start": v(30.6, -0.8) * mm, "end": v(31.74, -0.83) * mm});
            skArc(sketch, "E11.45.3", {"start": v(31.74, 0.83) * mm, "mid": v(32.28, 0.6) * mm, "end": v(32.8, 0.31) * mm});
            skArc(sketch, "E11.45.4", {"start": v(32.8, -0.31) * mm, "mid": v(32.8, -0.16) * mm, "end": v(32.8, 0) * mm});
            skArc(sketch, "E11.45.5", {"start": v(32.8, 0.31) * mm, "mid": v(32.8, 0.16) * mm, "end": v(32.8, 0) * mm});
            skArc(sketch, "E11.46.0", {"start": v(31.65, 2.5) * mm, "mid": v(32.17, 2.79) * mm, "end": v(32.66, 3.12) * mm});
            skLineSegment(sketch, "E11.46.1", {"start": v(30.35, 4) * mm, "end": v(31.48, 4.14) * mm});
            skLineSegment(sketch, "E11.46.2", {"start": v(30.51, 2.4) * mm, "end": v(31.65, 2.5) * mm});
            skArc(sketch, "E11.46.3", {"start": v(31.48, 4.14) * mm, "mid": v(32.04, 3.96) * mm, "end": v(32.6, 3.74) * mm});
            skArc(sketch, "E11.46.4", {"start": v(32.66, 3.12) * mm, "mid": v(32.64, 3.27) * mm, "end": v(32.62, 3.43) * mm});
            skArc(sketch, "E11.46.5", {"start": v(32.6, 3.74) * mm, "mid": v(32.6, 3.58) * mm, "end": v(32.62, 3.43) * mm});
            skArc(sketch, "E11.47.0", {"start": v(31.22, 5.79) * mm, "mid": v(31.7, 6.13) * mm, "end": v(32.15, 6.51) * mm});
            skLineSegment(sketch, "E11.47.1", {"start": v(29.76, 7.15) * mm, "end": v(30.87, 7.41) * mm});
            skLineSegment(sketch, "E11.47.2", {"start": v(30.1, 5.58) * mm, "end": v(31.22, 5.79) * mm});
            skArc(sketch, "E11.47.3", {"start": v(30.87, 7.41) * mm, "mid": v(31.45, 7.3) * mm, "end": v(32.02, 7.13) * mm});
            skArc(sketch, "E11.47.4", {"start": v(32.15, 6.51) * mm, "mid": v(32.12, 6.67) * mm, "end": v(32.09, 6.82) * mm});
            skArc(sketch, "E11.47.5", {"start": v(32.02, 7.13) * mm, "mid": v(32.05, 6.97) * mm, "end": v(32.09, 6.82) * mm});
            skArc(sketch, "E11.48.0", {"start": v(30.44, 9.02) * mm, "mid": v(30.88, 9.41) * mm, "end": v(31.3, 9.84) * mm});
            skLineSegment(sketch, "E11.48.1", {"start": v(28.85, 10.22) * mm, "end": v(29.93, 10.6) * mm});
            skLineSegment(sketch, "E11.48.2", {"start": v(29.35, 8.7) * mm, "end": v(30.44, 9.02) * mm});
            skArc(sketch, "E11.48.3", {"start": v(29.93, 10.6) * mm, "mid": v(30.52, 10.54) * mm, "end": v(31.1, 10.43) * mm});
            skArc(sketch, "E11.48.4", {"start": v(31.3, 9.84) * mm, "mid": v(31.25, 9.99) * mm, "end": v(31.2, 10.14) * mm});
            skArc(sketch, "E11.48.5", {"start": v(31.1, 10.43) * mm, "mid": v(31.15, 10.29) * mm, "end": v(31.2, 10.14) * mm});
            skArc(sketch, "E11.49.0", {"start": v(29.33, 12.15) * mm, "mid": v(29.73, 12.59) * mm, "end": v(30.1, 13.06) * mm});
            skLineSegment(sketch, "E11.49.1", {"start": v(27.63, 13.18) * mm, "end": v(28.66, 13.67) * mm});
            skLineSegment(sketch, "E11.49.2", {"start": v(28.28, 11.71) * mm, "end": v(29.33, 12.15) * mm});
            skArc(sketch, "E11.49.3", {"start": v(28.66, 13.67) * mm, "mid": v(29.25, 13.67) * mm, "end": v(29.84, 13.63) * mm});
            skArc(sketch, "E11.49.4", {"start": v(30.1, 13.06) * mm, "mid": v(30.03, 13.2) * mm, "end": v(29.97, 13.34) * mm});
            skArc(sketch, "E11.49.5", {"start": v(29.84, 13.63) * mm, "mid": v(29.9, 13.49) * mm, "end": v(29.97, 13.34) * mm});
            skArc(sketch, "E11.50.0", {"start": v(27.9, 15.15) * mm, "mid": v(28.25, 15.63) * mm, "end": v(28.56, 16.13) * mm});
            skLineSegment(sketch, "E11.50.1", {"start": v(26.1, 16) * mm, "end": v(27.07, 16.59) * mm});
            skLineSegment(sketch, "E11.50.2", {"start": v(26.9, 14.6) * mm, "end": v(27.9, 15.15) * mm});
            skArc(sketch, "E11.50.3", {"start": v(27.07, 16.59) * mm, "mid": v(27.66, 16.65) * mm, "end": v(28.25, 16.67) * mm});
            skArc(sketch, "E11.50.4", {"start": v(28.56, 16.13) * mm, "mid": v(28.49, 16.27) * mm, "end": v(28.4, 16.4) * mm});
            skArc(sketch, "E11.50.5", {"start": v(28.25, 16.67) * mm, "mid": v(28.33, 16.54) * mm, "end": v(28.4, 16.4) * mm});
            skArc(sketch, "E11.51.0", {"start": v(26.17, 17.98) * mm, "mid": v(26.46, 18.5) * mm, "end": v(26.72, 19.03) * mm});
            skLineSegment(sketch, "E11.51.1", {"start": v(24.28, 18.63) * mm, "end": v(25.19, 19.33) * mm});
            skLineSegment(sketch, "E11.51.2", {"start": v(25.22, 17.34) * mm, "end": v(26.17, 17.98) * mm});
            skArc(sketch, "E11.51.3", {"start": v(25.19, 19.33) * mm, "mid": v(25.77, 19.45) * mm, "end": v(26.35, 19.53) * mm});
            skArc(sketch, "E11.51.4", {"start": v(26.72, 19.03) * mm, "mid": v(26.63, 19.15) * mm, "end": v(26.54, 19.28) * mm});
            skArc(sketch, "E11.51.5", {"start": v(26.35, 19.53) * mm, "mid": v(26.45, 19.4) * mm, "end": v(26.54, 19.28) * mm});
            skArc(sketch, "E11.52.0", {"start": v(24.14, 20.62) * mm, "mid": v(24.39, 21.16) * mm, "end": v(24.59, 21.72) * mm});
            skLineSegment(sketch, "E11.52.1", {"start": v(22.2, 21.07) * mm, "end": v(23.03, 21.86) * mm});
            skLineSegment(sketch, "E11.52.2", {"start": v(23.27, 19.88) * mm, "end": v(24.14, 20.62) * mm});
            skArc(sketch, "E11.52.3", {"start": v(23.03, 21.86) * mm, "mid": v(23.6, 22.04) * mm, "end": v(24.17, 22.18) * mm});
            skArc(sketch, "E11.52.4", {"start": v(24.59, 21.72) * mm, "mid": v(24.48, 21.83) * mm, "end": v(24.38, 21.95) * mm});
            skArc(sketch, "E11.52.5", {"start": v(24.17, 22.18) * mm, "mid": v(24.27, 22.07) * mm, "end": v(24.38, 21.95) * mm});
            skArc(sketch, "E11.53.0", {"start": v(21.86, 23.03) * mm, "mid": v(22.04, 23.6) * mm, "end": v(22.18, 24.17) * mm});
            skLineSegment(sketch, "E11.53.1", {"start": v(19.88, 23.27) * mm, "end": v(20.62, 24.14) * mm});
            skLineSegment(sketch, "E11.53.2", {"start": v(21.07, 22.2) * mm, "end": v(21.86, 23.03) * mm});
            skArc(sketch, "E11.53.3", {"start": v(20.62, 24.14) * mm, "mid": v(21.16, 24.39) * mm, "end": v(21.72, 24.59) * mm});
            skArc(sketch, "E11.53.4", {"start": v(22.18, 24.17) * mm, "mid": v(22.07, 24.27) * mm, "end": v(21.95, 24.38) * mm});
            skArc(sketch, "E11.53.5", {"start": v(21.72, 24.59) * mm, "mid": v(21.83, 24.48) * mm, "end": v(21.95, 24.38) * mm});
            skArc(sketch, "E11.54.0", {"start": v(19.33, 25.19) * mm, "mid": v(19.45, 25.77) * mm, "end": v(19.53, 26.35) * mm});
            skLineSegment(sketch, "E11.54.1", {"start": v(17.34, 25.22) * mm, "end": v(17.98, 26.17) * mm});
            skLineSegment(sketch, "E11.54.2", {"start": v(18.63, 24.28) * mm, "end": v(19.33, 25.19) * mm});
            skArc(sketch, "E11.54.3", {"start": v(17.98, 26.17) * mm, "mid": v(18.5, 26.46) * mm, "end": v(19.03, 26.72) * mm});
            skArc(sketch, "E11.54.4", {"start": v(19.53, 26.35) * mm, "mid": v(19.4, 26.45) * mm, "end": v(19.28, 26.54) * mm});
            skArc(sketch, "E11.54.5", {"start": v(19.03, 26.72) * mm, "mid": v(19.15, 26.63) * mm, "end": v(19.28, 26.54) * mm});
            skArc(sketch, "E11.55.0", {"start": v(16.59, 27.07) * mm, "mid": v(16.65, 27.66) * mm, "end": v(16.67, 28.25) * mm});
            skLineSegment(sketch, "E11.55.1", {"start": v(14.6, 26.9) * mm, "end": v(15.15, 27.9) * mm});
            skLineSegment(sketch, "E11.55.2", {"start": v(16, 26.1) * mm, "end": v(16.59, 27.07) * mm});
            skArc(sketch, "E11.55.3", {"start": v(15.15, 27.9) * mm, "mid": v(15.63, 28.25) * mm, "end": v(16.13, 28.56) * mm});
            skArc(sketch, "E11.55.4", {"start": v(16.67, 28.25) * mm, "mid": v(16.54, 28.33) * mm, "end": v(16.4, 28.4) * mm});
            skArc(sketch, "E11.55.5", {"start": v(16.13, 28.56) * mm, "mid": v(16.27, 28.49) * mm, "end": v(16.4, 28.4) * mm});
            skArc(sketch, "E11.56.0", {"start": v(13.67, 28.66) * mm, "mid": v(13.67, 29.25) * mm, "end": v(13.63, 29.84) * mm});
            skLineSegment(sketch, "E11.56.1", {"start": v(11.71, 28.28) * mm, "end": v(12.15, 29.33) * mm});
            skLineSegment(sketch, "E11.56.2", {"start": v(13.18, 27.63) * mm, "end": v(13.67, 28.66) * mm});
            skArc(sketch, "E11.56.3", {"start": v(12.15, 29.33) * mm, "mid": v(12.59, 29.73) * mm, "end": v(13.06, 30.1) * mm});
            skArc(sketch, "E11.56.4", {"start": v(13.63, 29.84) * mm, "mid": v(13.49, 29.9) * mm, "end": v(13.34, 29.97) * mm});
            skArc(sketch, "E11.56.5", {"start": v(13.06, 30.1) * mm, "mid": v(13.2, 30.03) * mm, "end": v(13.34, 29.97) * mm});
            skArc(sketch, "E11.57.0", {"start": v(10.6, 29.93) * mm, "mid": v(10.54, 30.52) * mm, "end": v(10.43, 31.1) * mm});
            skLineSegment(sketch, "E11.57.1", {"start": v(8.7, 29.35) * mm, "end": v(9.02, 30.44) * mm});
            skLineSegment(sketch, "E11.57.2", {"start": v(10.22, 28.85) * mm, "end": v(10.6, 29.93) * mm});
            skArc(sketch, "E11.57.3", {"start": v(9.02, 30.44) * mm, "mid": v(9.41, 30.88) * mm, "end": v(9.84, 31.3) * mm});
            skArc(sketch, "E11.57.4", {"start": v(10.43, 31.1) * mm, "mid": v(10.29, 31.15) * mm, "end": v(10.14, 31.2) * mm});
            skArc(sketch, "E11.57.5", {"start": v(9.84, 31.3) * mm, "mid": v(9.99, 31.25) * mm, "end": v(10.14, 31.2) * mm});
            skArc(sketch, "E11.58.0", {"start": v(7.41, 30.87) * mm, "mid": v(7.3, 31.45) * mm, "end": v(7.13, 32.02) * mm});
            skLineSegment(sketch, "E11.58.1", {"start": v(5.58, 30.1) * mm, "end": v(5.79, 31.22) * mm});
            skLineSegment(sketch, "E11.58.2", {"start": v(7.15, 29.76) * mm, "end": v(7.41, 30.87) * mm});
            skArc(sketch, "E11.58.3", {"start": v(5.79, 31.22) * mm, "mid": v(6.13, 31.7) * mm, "end": v(6.51, 32.15) * mm});
            skArc(sketch, "E11.58.4", {"start": v(7.13, 32.02) * mm, "mid": v(6.97, 32.05) * mm, "end": v(6.82, 32.09) * mm});
            skArc(sketch, "E11.58.5", {"start": v(6.51, 32.15) * mm, "mid": v(6.67, 32.12) * mm, "end": v(6.82, 32.09) * mm});
            skArc(sketch, "E11.59.0", {"start": v(4.14, 31.48) * mm, "mid": v(3.96, 32.04) * mm, "end": v(3.74, 32.6) * mm});
            skLineSegment(sketch, "E11.59.1", {"start": v(2.4, 30.51) * mm, "end": v(2.5, 31.65) * mm});
            skLineSegment(sketch, "E11.59.2", {"start": v(4, 30.35) * mm, "end": v(4.14, 31.48) * mm});
            skArc(sketch, "E11.59.3", {"start": v(2.5, 31.65) * mm, "mid": v(2.79, 32.17) * mm, "end": v(3.12, 32.66) * mm});
            skArc(sketch, "E11.59.4", {"start": v(3.74, 32.6) * mm, "mid": v(3.58, 32.6) * mm, "end": v(3.43, 32.62) * mm});
            skArc(sketch, "E11.59.5", {"start": v(3.12, 32.66) * mm, "mid": v(3.27, 32.64) * mm, "end": v(3.43, 32.62) * mm});
            skSolve(sketch);
        }
        {
            var Q0;
            Q0=makeQuery(id+"F0.imprint","IMPRINT",FACE,{"disambiguationData":[TD([[makeQuery(id+"F0.imprint","IMPRINT",EDGE,{"derivedFrom":sQuery(id+"F0.wireOp",EDGE,"E11.37.0")}),1.0]])]});
            var Q1;
            Q1=makeQuery(id+"F0.imprint","IMPRINT",FACE,{"disambiguationData":[TD([[makeQuery(id+"F0.imprint","IMPRINT",EDGE,{"derivedFrom":sQuery(id+"F0.wireOp",EDGE,"E11.6.0")}),1.0]])]});
            var Q2;
            Q2=makeQuery(id+"F0.imprint","IMPRINT",FACE,{"disambiguationData":[TD([[makeQuery(id+"F0.imprint","IMPRINT",EDGE,{"derivedFrom":sQuery(id+"F0.wireOp",EDGE,"E11.38.0")}),1.0]])]});
            var Q3;
            Q3=makeQuery(id+"F0.imprint","IMPRINT",FACE,{"disambiguationData":[TD([[makeQuery(id+"F0.imprint","IMPRINT",EDGE,{"derivedFrom":sQuery(id+"F0.wireOp",EDGE,"E11.39.0")}),1.0]])]});
            var Q4;
            Q4=makeQuery(id+"F0.imprint","IMPRINT",FACE,{"disambiguationData":[TD([[makeQuery(id+"F0.imprint","IMPRINT",EDGE,{"derivedFrom":sQuery(id+"F0.wireOp",EDGE,"E11.40.0")}),1.0]])]});
            var Q5;
            Q5=makeQuery(id+"F0.imprint","IMPRINT",FACE,{"disambiguationData":[TD([[makeQuery(id+"F0.imprint","IMPRINT",EDGE,{"derivedFrom":sQuery(id+"F0.wireOp",EDGE,"E1")}),1.0]])]});
            var Q6;
            Q6=makeQuery(id+"F0.imprint","IMPRINT",FACE,{"disambiguationData":[TD([[makeQuery(id+"F0.imprint","IMPRINT",EDGE,{"derivedFrom":sQuery(id+"F0.wireOp",EDGE,"E11.50.0")}),1.0]])]});
            var Q7;
            Q7=makeQuery(id+"F0.imprint","IMPRINT",FACE,{"disambiguationData":[TD([[makeQuery(id+"F0.imprint","IMPRINT",EDGE,{"derivedFrom":sQuery(id+"F0.wireOp",EDGE,"E11.51.0")}),1.0]])]});
            var Q8;
            Q8=makeQuery(id+"F0.imprint","IMPRINT",FACE,{"disambiguationData":[TD([[makeQuery(id+"F0.imprint","IMPRINT",EDGE,{"derivedFrom":sQuery(id+"F0.wireOp",EDGE,"E11.52.0")}),1.0]])]});
            var Q9;
            Q9=makeQuery(id+"F0.imprint","IMPRINT",FACE,{"disambiguationData":[TD([[makeQuery(id+"F0.imprint","IMPRINT",EDGE,{"derivedFrom":sQuery(id+"F0.wireOp",EDGE,"E11.53.0")}),1.0]])]});
            var Q10;
            Q10=makeQuery(id+"F0.imprint","IMPRINT",FACE,{"disambiguationData":[TD([[makeQuery(id+"F0.imprint","IMPRINT",EDGE,{"derivedFrom":sQuery(id+"F0.wireOp",EDGE,"E11.54.0")}),1.0]])]});
            var Q11;
            Q11=makeQuery(id+"F0.imprint","IMPRINT",FACE,{"disambiguationData":[TD([[makeQuery(id+"F0.imprint","IMPRINT",EDGE,{"derivedFrom":sQuery(id+"F0.wireOp",EDGE,"E11.2.0")}),1.0]])]});
            var Q12;
            Q12=makeQuery(id+"F0.imprint","IMPRINT",FACE,{"disambiguationData":[TD([[makeQuery(id+"F0.imprint","IMPRINT",EDGE,{"derivedFrom":sQuery(id+"F0.wireOp",EDGE,"E11.3.0")}),1.0]])]});
            var Q13;
            Q13=makeQuery(id+"F0.imprint","IMPRINT",FACE,{"disambiguationData":[TD([[makeQuery(id+"F0.imprint","IMPRINT",EDGE,{"derivedFrom":sQuery(id+"F0.wireOp",EDGE,"E11.4.0")}),1.0]])]});
            var Q14;
            Q14=makeQuery(id+"F0.imprint","IMPRINT",FACE,{"disambiguationData":[TD([[makeQuery(id+"F0.imprint","IMPRINT",EDGE,{"derivedFrom":sQuery(id+"F0.wireOp",EDGE,"E11.5.0")}),1.0]])]});
            var Q15;
            Q15=makeQuery(id+"F0.imprint","IMPRINT",FACE,{"disambiguationData":[TD([[makeQuery(id+"F0.imprint","IMPRINT",EDGE,{"derivedFrom":sQuery(id+"F0.wireOp",EDGE,"E11.41.0")}),1.0]])]});
            var Q16;
            Q16=makeQuery(id+"F0.imprint","IMPRINT",FACE,{"disambiguationData":[TD([[makeQuery(id+"F0.imprint","IMPRINT",EDGE,{"derivedFrom":sQuery(id+"F0.wireOp",EDGE,"E11.1.0")}),1.0]])]});
            var Q17;
            Q17=makeQuery(id+"F0.imprint","IMPRINT",FACE,{"disambiguationData":[TD([[makeQuery(id+"F0.imprint","IMPRINT",EDGE,{"derivedFrom":sQuery(id+"F0.wireOp",EDGE,"E11.59.0")}),1.0]])]});
            var Q18;
            Q18=makeQuery(id+"F0.imprint","IMPRINT",FACE,{"disambiguationData":[TD([[makeQuery(id+"F0.imprint","IMPRINT",EDGE,{"derivedFrom":sQuery(id+"F0.wireOp",EDGE,"E11.49.0")}),1.0]])]});
            var Q19;
            Q19=makeQuery(id+"F0.imprint","IMPRINT",FACE,{"disambiguationData":[TD([[makeQuery(id+"F0.imprint","IMPRINT",EDGE,{"derivedFrom":sQuery(id+"F0.wireOp",EDGE,"E11.55.0")}),1.0]])]});
            var Q20;
            Q20=makeQuery(id+"F0.imprint","IMPRINT",FACE,{"disambiguationData":[TD([[makeQuery(id+"F0.imprint","IMPRINT",EDGE,{"derivedFrom":sQuery(id+"F0.wireOp",EDGE,"E11.56.0")}),1.0]])]});
            var Q21;
            Q21=makeQuery(id+"F0.imprint","IMPRINT",FACE,{"disambiguationData":[TD([[makeQuery(id+"F0.imprint","IMPRINT",EDGE,{"derivedFrom":sQuery(id+"F0.wireOp",EDGE,"E11.57.0")}),1.0]])]});
            var Q22;
            Q22=makeQuery(id+"F0.imprint","IMPRINT",FACE,{"disambiguationData":[TD([[makeQuery(id+"F0.imprint","IMPRINT",EDGE,{"derivedFrom":sQuery(id+"F0.wireOp",EDGE,"E11.58.0")}),1.0]])]});
            var Q23;
            Q23=makeQuery(id+"F0.imprint","IMPRINT",FACE,{"disambiguationData":[TD([[makeQuery(id+"F0.imprint","IMPRINT",EDGE,{"derivedFrom":sQuery(id+"F0.wireOp",EDGE,"E11.17.0")}),1.0]])]});
            var Q24;
            Q24=makeQuery(id+"F0.imprint","IMPRINT",FACE,{"disambiguationData":[TD([[makeQuery(id+"F0.imprint","IMPRINT",EDGE,{"derivedFrom":sQuery(id+"F0.wireOp",EDGE,"E11.35.0")}),1.0]])]});
            var Q25;
            Q25=makeQuery(id+"F0.imprint","IMPRINT",FACE,{"disambiguationData":[TD([[makeQuery(id+"F0.imprint","IMPRINT",EDGE,{"derivedFrom":sQuery(id+"F0.wireOp",EDGE,"E11.21.0")}),1.0]])]});
            var Q26;
            Q26=makeQuery(id+"F0.imprint","IMPRINT",FACE,{"disambiguationData":[TD([[makeQuery(id+"F0.imprint","IMPRINT",EDGE,{"derivedFrom":sQuery(id+"F0.wireOp",EDGE,"E11.22.0")}),1.0]])]});
            var Q27;
            Q27=makeQuery(id+"F0.imprint","IMPRINT",FACE,{"disambiguationData":[TD([[makeQuery(id+"F0.imprint","IMPRINT",EDGE,{"derivedFrom":sQuery(id+"F0.wireOp",EDGE,"E11.7.0")}),1.0]])]});
            var Q28;
            Q28=makeQuery(id+"F0.imprint","IMPRINT",FACE,{"disambiguationData":[TD([[makeQuery(id+"F0.imprint","IMPRINT",EDGE,{"derivedFrom":sQuery(id+"F0.wireOp",EDGE,"E11.23.0")}),1.0]])]});
            var Q29;
            Q29=makeQuery(id+"F0.imprint","IMPRINT",FACE,{"disambiguationData":[TD([[makeQuery(id+"F0.imprint","IMPRINT",EDGE,{"derivedFrom":sQuery(id+"F0.wireOp",EDGE,"E11.8.0")}),1.0]])]});
            var Q30;
            Q30=makeQuery(id+"F0.imprint","IMPRINT",FACE,{"disambiguationData":[TD([[makeQuery(id+"F0.imprint","IMPRINT",EDGE,{"derivedFrom":sQuery(id+"F0.wireOp",EDGE,"E11.25.0")}),1.0]])]});
            var Q31;
            Q31=makeQuery(id+"F0.imprint","IMPRINT",FACE,{"disambiguationData":[TD([[makeQuery(id+"F0.imprint","IMPRINT",EDGE,{"derivedFrom":sQuery(id+"F0.wireOp",EDGE,"E11.9.0")}),1.0]])]});
            var Q32;
            Q32=makeQuery(id+"F0.imprint","IMPRINT",FACE,{"disambiguationData":[TD([[makeQuery(id+"F0.imprint","IMPRINT",EDGE,{"derivedFrom":sQuery(id+"F0.wireOp",EDGE,"E11.43.0")}),1.0]])]});
            var Q33;
            {var subQ0=sQuery(id+"F0.wireOp",EDGE,"E0");var subQ26=makeQuery(id+"F0.imprint","INTERSECT",VERTEX,{"derivedFrom":[subQ0,sQuery(id+"F0.wireOp",EDGE,"E11.45.1")]});Q33=makeQuery(id+"F0.imprint","IMPRINT",FACE,{"disambiguationData":[TD([[makeQuery(id+"F0.imprint","IMPRINT",EDGE,{"disambiguationData":[TD([[subQ26,-1.0]])],"derivedFrom":subQ0}),1.0]])]});}
            var Q34;
            Q34=makeQuery(id+"F0.imprint","IMPRINT",FACE,{"disambiguationData":[TD([[makeQuery(id+"F0.imprint","IMPRINT",EDGE,{"derivedFrom":sQuery(id+"F0.wireOp",EDGE,"E11.30.0")}),1.0]])]});
            var Q35;
            Q35=makeQuery(id+"F0.imprint","IMPRINT",FACE,{"disambiguationData":[TD([[makeQuery(id+"F0.imprint","IMPRINT",EDGE,{"derivedFrom":sQuery(id+"F0.wireOp",EDGE,"E11.14.0")}),1.0]])]});
            var Q36;
            Q36=makeQuery(id+"F0.imprint","IMPRINT",FACE,{"disambiguationData":[TD([[makeQuery(id+"F0.imprint","IMPRINT",EDGE,{"derivedFrom":sQuery(id+"F0.wireOp",EDGE,"E11.33.0")}),1.0]])]});
            var Q37;
            Q37=makeQuery(id+"F0.imprint","IMPRINT",FACE,{"disambiguationData":[TD([[makeQuery(id+"F0.imprint","IMPRINT",EDGE,{"derivedFrom":sQuery(id+"F0.wireOp",EDGE,"E11.31.0")}),1.0]])]});
            var Q38;
            Q38=makeQuery(id+"F0.imprint","IMPRINT",FACE,{"disambiguationData":[TD([[makeQuery(id+"F0.imprint","IMPRINT",EDGE,{"derivedFrom":sQuery(id+"F0.wireOp",EDGE,"E11.15.0")}),1.0]])]});
            var Q39;
            Q39=makeQuery(id+"F0.imprint","IMPRINT",FACE,{"disambiguationData":[TD([[makeQuery(id+"F0.imprint","IMPRINT",EDGE,{"derivedFrom":sQuery(id+"F0.wireOp",EDGE,"E11.32.0")}),1.0]])]});
            var Q40;
            Q40=makeQuery(id+"F0.imprint","IMPRINT",FACE,{"disambiguationData":[TD([[makeQuery(id+"F0.imprint","IMPRINT",EDGE,{"derivedFrom":sQuery(id+"F0.wireOp",EDGE,"E11.16.0")}),1.0]])]});
            var Q41;
            Q41=makeQuery(id+"F0.imprint","IMPRINT",FACE,{"disambiguationData":[TD([[makeQuery(id+"F0.imprint","IMPRINT",EDGE,{"derivedFrom":sQuery(id+"F0.wireOp",EDGE,"E11.34.0")}),1.0]])]});
            var Q42;
            Q42=makeQuery(id+"F0.imprint","IMPRINT",FACE,{"disambiguationData":[TD([[makeQuery(id+"F0.imprint","IMPRINT",EDGE,{"derivedFrom":sQuery(id+"F0.wireOp",EDGE,"E11.18.0")}),1.0]])]});
            var Q43;
            Q43=makeQuery(id+"F0.imprint","IMPRINT",FACE,{"disambiguationData":[TD([[makeQuery(id+"F0.imprint","IMPRINT",EDGE,{"derivedFrom":sQuery(id+"F0.wireOp",EDGE,"E11.19.0")}),1.0]])]});
            var Q44;
            Q44=makeQuery(id+"F0.imprint","IMPRINT",FACE,{"disambiguationData":[TD([[makeQuery(id+"F0.imprint","IMPRINT",EDGE,{"derivedFrom":sQuery(id+"F0.wireOp",EDGE,"E11.36.0")}),1.0]])]});
            var Q45;
            Q45=makeQuery(id+"F0.imprint","IMPRINT",FACE,{"disambiguationData":[TD([[makeQuery(id+"F0.imprint","IMPRINT",EDGE,{"derivedFrom":sQuery(id+"F0.wireOp",EDGE,"E11.20.0")}),1.0]])]});
            var Q46;
            Q46=makeQuery(id+"F0.imprint","IMPRINT",FACE,{"disambiguationData":[TD([[makeQuery(id+"F0.imprint","IMPRINT",EDGE,{"derivedFrom":sQuery(id+"F0.wireOp",EDGE,"E11.24.0")}),1.0]])]});
            var Q47;
            Q47=makeQuery(id+"F0.imprint","IMPRINT",FACE,{"disambiguationData":[TD([[makeQuery(id+"F0.imprint","IMPRINT",EDGE,{"derivedFrom":sQuery(id+"F0.wireOp",EDGE,"E11.42.0")}),1.0]])]});
            var Q48;
            Q48=makeQuery(id+"F0.imprint","IMPRINT",FACE,{"disambiguationData":[TD([[makeQuery(id+"F0.imprint","IMPRINT",EDGE,{"derivedFrom":sQuery(id+"F0.wireOp",EDGE,"E11.26.0")}),1.0]])]});
            var Q49;
            Q49=makeQuery(id+"F0.imprint","IMPRINT",FACE,{"disambiguationData":[TD([[makeQuery(id+"F0.imprint","IMPRINT",EDGE,{"derivedFrom":sQuery(id+"F0.wireOp",EDGE,"E11.10.0")}),1.0]])]});
            var Q50;
            Q50=makeQuery(id+"F0.imprint","IMPRINT",FACE,{"disambiguationData":[TD([[makeQuery(id+"F0.imprint","IMPRINT",EDGE,{"derivedFrom":sQuery(id+"F0.wireOp",EDGE,"E11.27.0")}),1.0]])]});
            var Q51;
            Q51=makeQuery(id+"F0.imprint","IMPRINT",FACE,{"disambiguationData":[TD([[makeQuery(id+"F0.imprint","IMPRINT",EDGE,{"derivedFrom":sQuery(id+"F0.wireOp",EDGE,"E11.11.0")}),1.0]])]});
            var Q52;
            Q52=makeQuery(id+"F0.imprint","IMPRINT",FACE,{"disambiguationData":[TD([[makeQuery(id+"F0.imprint","IMPRINT",EDGE,{"derivedFrom":sQuery(id+"F0.wireOp",EDGE,"E11.44.0")}),1.0]])]});
            var Q53;
            Q53=makeQuery(id+"F0.imprint","IMPRINT",FACE,{"disambiguationData":[TD([[makeQuery(id+"F0.imprint","IMPRINT",EDGE,{"derivedFrom":sQuery(id+"F0.wireOp",EDGE,"E11.28.0")}),1.0]])]});
            var Q54;
            Q54=makeQuery(id+"F0.imprint","IMPRINT",FACE,{"disambiguationData":[TD([[makeQuery(id+"F0.imprint","IMPRINT",EDGE,{"derivedFrom":sQuery(id+"F0.wireOp",EDGE,"E11.12.0")}),1.0]])]});
            var Q55;
            Q55=makeQuery(id+"F0.imprint","IMPRINT",FACE,{"disambiguationData":[TD([[makeQuery(id+"F0.imprint","IMPRINT",EDGE,{"derivedFrom":sQuery(id+"F0.wireOp",EDGE,"E11.29.0")}),1.0]])]});
            var Q56;
            Q56=makeQuery(id+"F0.imprint","IMPRINT",FACE,{"disambiguationData":[TD([[makeQuery(id+"F0.imprint","IMPRINT",EDGE,{"derivedFrom":sQuery(id+"F0.wireOp",EDGE,"E11.13.0")}),1.0]])]});
            var Q57;
            Q57=makeQuery(id+"F0.imprint","IMPRINT",FACE,{"disambiguationData":[TD([[makeQuery(id+"F0.imprint","IMPRINT",EDGE,{"derivedFrom":sQuery(id+"F0.wireOp",EDGE,"E11.46.0")}),1.0]])]});
            var Q58;
            Q58=makeQuery(id+"F0.imprint","IMPRINT",FACE,{"disambiguationData":[TD([[makeQuery(id+"F0.imprint","IMPRINT",EDGE,{"derivedFrom":sQuery(id+"F0.wireOp",EDGE,"E11.47.0")}),1.0]])]});
            var Q59;
            Q59=makeQuery(id+"F0.imprint","IMPRINT",FACE,{"disambiguationData":[TD([[makeQuery(id+"F0.imprint","IMPRINT",EDGE,{"derivedFrom":sQuery(id+"F0.wireOp",EDGE,"E11.48.0")}),1.0]])]});
            var Q60;
            Q60=makeQuery(id+"F0.imprint","IMPRINT",FACE,{"disambiguationData":[TD([[makeQuery(id+"F0.imprint","IMPRINT",EDGE,{"derivedFrom":sQuery(id+"F0.wireOp",EDGE,"E11.45.0")}),1.0]])]});
            extrude(context, id + "F1", {"entities" : qUnion([Q0, Q1, Q2, Q3, Q4, Q5, Q6, Q7, Q8, Q9, Q10, Q11, Q12, Q13, Q14, Q15, Q16, Q17, Q18, Q19, Q20, Q21, Q22, Q23, Q24, Q25, Q26, Q27, Q28, Q29, Q30, Q31, Q32, Q33, Q34, Q35, Q36, Q37, Q38, Q39, Q40, Q41, Q42, Q43, Q44, Q45, Q46, Q47, Q48, Q49, Q50, Q51, Q52, Q53, Q54, Q55, Q56, Q57, Q58, Q59, Q60]), "depth" : 6.35 * mm});
        }
        {
            var Q0;
            Q0=makeQuery(id+"F1.opExtrude","CAP_FACE",FACE,{"disambiguationData":[OSD([sQuery(id+"F0.wireOp",EDGE,"E0"),sQuery(id+"F0.wireOp",EDGE,"E1"),sQuery(id+"F0.wireOp",EDGE,"E2"),sQuery(id+"F0.wireOp",EDGE,"E4.trimOffspring"),sQuery(id+"F0.wireOp",EDGE,"E6.MirrorCS"),sQuery(id+"F0.wireOp",EDGE,"E9.MirrorCS"),sQuery(id+"F0.wireOp",EDGE,"E10.MirrorCS"),sQuery(id+"F0.wireOp",EDGE,"E11.1.0"),sQuery(id+"F0.wireOp",EDGE,"E11.1.1"),sQuery(id+"F0.wireOp",EDGE,"E11.1.2"),sQuery(id+"F0.wireOp",EDGE,"E11.1.3"),sQuery(id+"F0.wireOp",EDGE,"E11.1.4"),sQuery(id+"F0.wireOp",EDGE,"E11.1.5"),sQuery(id+"F0.wireOp",EDGE,"E11.2.0"),sQuery(id+"F0.wireOp",EDGE,"E11.2.1"),sQuery(id+"F0.wireOp",EDGE,"E11.2.2"),sQuery(id+"F0.wireOp",EDGE,"E11.2.3"),sQuery(id+"F0.wireOp",EDGE,"E11.2.4"),sQuery(id+"F0.wireOp",EDGE,"E11.2.5"),sQuery(id+"F0.wireOp",EDGE,"E11.3.0"),sQuery(id+"F0.wireOp",EDGE,"E11.3.1"),sQuery(id+"F0.wireOp",EDGE,"E11.3.2"),sQuery(id+"F0.wireOp",EDGE,"E11.3.3"),sQuery(id+"F0.wireOp",EDGE,"E11.3.4"),sQuery(id+"F0.wireOp",EDGE,"E11.3.5"),sQuery(id+"F0.wireOp",EDGE,"E11.4.0"),sQuery(id+"F0.wireOp",EDGE,"E11.4.1"),sQuery(id+"F0.wireOp",EDGE,"E11.4.2"),sQuery(id+"F0.wireOp",EDGE,"E11.4.3"),sQuery(id+"F0.wireOp",EDGE,"E11.4.4"),sQuery(id+"F0.wireOp",EDGE,"E11.4.5"),sQuery(id+"F0.wireOp",EDGE,"E11.5.0"),sQuery(id+"F0.wireOp",EDGE,"E11.5.1"),sQuery(id+"F0.wireOp",EDGE,"E11.5.2"),sQuery(id+"F0.wireOp",EDGE,"E11.5.3"),sQuery(id+"F0.wireOp",EDGE,"E11.5.4"),sQuery(id+"F0.wireOp",EDGE,"E11.5.5"),sQuery(id+"F0.wireOp",EDGE,"E11.6.0"),sQuery(id+"F0.wireOp",EDGE,"E11.6.1"),sQuery(id+"F0.wireOp",EDGE,"E11.6.2"),sQuery(id+"F0.wireOp",EDGE,"E11.6.3"),sQuery(id+"F0.wireOp",EDGE,"E11.6.4"),sQuery(id+"F0.wireOp",EDGE,"E11.6.5"),sQuery(id+"F0.wireOp",EDGE,"E11.7.0"),sQuery(id+"F0.wireOp",EDGE,"E11.7.1"),sQuery(id+"F0.wireOp",EDGE,"E11.7.2"),sQuery(id+"F0.wireOp",EDGE,"E11.7.3"),sQuery(id+"F0.wireOp",EDGE,"E11.7.4"),sQuery(id+"F0.wireOp",EDGE,"E11.7.5"),sQuery(id+"F0.wireOp",EDGE,"E11.8.0"),sQuery(id+"F0.wireOp",EDGE,"E11.8.1"),sQuery(id+"F0.wireOp",EDGE,"E11.8.2"),sQuery(id+"F0.wireOp",EDGE,"E11.8.3"),sQuery(id+"F0.wireOp",EDGE,"E11.8.4"),sQuery(id+"F0.wireOp",EDGE,"E11.8.5"),sQuery(id+"F0.wireOp",EDGE,"E11.9.0"),sQuery(id+"F0.wireOp",EDGE,"E11.9.1"),sQuery(id+"F0.wireOp",EDGE,"E11.9.2"),sQuery(id+"F0.wireOp",EDGE,"E11.9.3"),sQuery(id+"F0.wireOp",EDGE,"E11.9.4"),sQuery(id+"F0.wireOp",EDGE,"E11.9.5"),sQuery(id+"F0.wireOp",EDGE,"E11.10.0"),sQuery(id+"F0.wireOp",EDGE,"E11.10.1"),sQuery(id+"F0.wireOp",EDGE,"E11.10.2"),sQuery(id+"F0.wireOp",EDGE,"E11.10.3"),sQuery(id+"F0.wireOp",EDGE,"E11.10.4"),sQuery(id+"F0.wireOp",EDGE,"E11.10.5"),sQuery(id+"F0.wireOp",EDGE,"E11.11.0"),sQuery(id+"F0.wireOp",EDGE,"E11.11.1"),sQuery(id+"F0.wireOp",EDGE,"E11.11.2"),sQuery(id+"F0.wireOp",EDGE,"E11.11.3"),sQuery(id+"F0.wireOp",EDGE,"E11.11.4"),sQuery(id+"F0.wireOp",EDGE,"E11.11.5"),sQuery(id+"F0.wireOp",EDGE,"E11.12.0"),sQuery(id+"F0.wireOp",EDGE,"E11.12.1"),sQuery(id+"F0.wireOp",EDGE,"E11.12.2"),sQuery(id+"F0.wireOp",EDGE,"E11.12.3"),sQuery(id+"F0.wireOp",EDGE,"E11.12.4"),sQuery(id+"F0.wireOp",EDGE,"E11.12.5"),sQuery(id+"F0.wireOp",EDGE,"E11.13.0"),sQuery(id+"F0.wireOp",EDGE,"E11.13.1"),sQuery(id+"F0.wireOp",EDGE,"E11.13.2"),sQuery(id+"F0.wireOp",EDGE,"E11.13.3"),sQuery(id+"F0.wireOp",EDGE,"E11.13.4"),sQuery(id+"F0.wireOp",EDGE,"E11.13.5"),sQuery(id+"F0.wireOp",EDGE,"E11.14.0"),sQuery(id+"F0.wireOp",EDGE,"E11.14.1"),sQuery(id+"F0.wireOp",EDGE,"E11.14.2"),sQuery(id+"F0.wireOp",EDGE,"E11.14.3"),sQuery(id+"F0.wireOp",EDGE,"E11.14.4"),sQuery(id+"F0.wireOp",EDGE,"E11.14.5"),sQuery(id+"F0.wireOp",EDGE,"E11.15.0"),sQuery(id+"F0.wireOp",EDGE,"E11.15.1"),sQuery(id+"F0.wireOp",EDGE,"E11.15.2"),sQuery(id+"F0.wireOp",EDGE,"E11.15.3"),sQuery(id+"F0.wireOp",EDGE,"E11.15.4"),sQuery(id+"F0.wireOp",EDGE,"E11.15.5"),sQuery(id+"F0.wireOp",EDGE,"E11.16.0"),sQuery(id+"F0.wireOp",EDGE,"E11.16.1"),sQuery(id+"F0.wireOp",EDGE,"E11.16.2"),sQuery(id+"F0.wireOp",EDGE,"E11.16.3"),sQuery(id+"F0.wireOp",EDGE,"E11.16.4"),sQuery(id+"F0.wireOp",EDGE,"E11.16.5"),sQuery(id+"F0.wireOp",EDGE,"E11.17.0"),sQuery(id+"F0.wireOp",EDGE,"E11.17.1"),sQuery(id+"F0.wireOp",EDGE,"E11.17.2"),sQuery(id+"F0.wireOp",EDGE,"E11.17.3"),sQuery(id+"F0.wireOp",EDGE,"E11.17.4"),sQuery(id+"F0.wireOp",EDGE,"E11.17.5"),sQuery(id+"F0.wireOp",EDGE,"E11.18.0"),sQuery(id+"F0.wireOp",EDGE,"E11.18.1"),sQuery(id+"F0.wireOp",EDGE,"E11.18.2"),sQuery(id+"F0.wireOp",EDGE,"E11.18.3"),sQuery(id+"F0.wireOp",EDGE,"E11.18.4"),sQuery(id+"F0.wireOp",EDGE,"E11.18.5"),sQuery(id+"F0.wireOp",EDGE,"E11.19.0"),sQuery(id+"F0.wireOp",EDGE,"E11.19.1"),sQuery(id+"F0.wireOp",EDGE,"E11.19.2"),sQuery(id+"F0.wireOp",EDGE,"E11.19.3"),sQuery(id+"F0.wireOp",EDGE,"E11.19.4"),sQuery(id+"F0.wireOp",EDGE,"E11.19.5"),sQuery(id+"F0.wireOp",EDGE,"E11.20.0"),sQuery(id+"F0.wireOp",EDGE,"E11.20.1"),sQuery(id+"F0.wireOp",EDGE,"E11.20.2"),sQuery(id+"F0.wireOp",EDGE,"E11.20.3"),sQuery(id+"F0.wireOp",EDGE,"E11.20.4"),sQuery(id+"F0.wireOp",EDGE,"E11.20.5"),sQuery(id+"F0.wireOp",EDGE,"E11.21.0"),sQuery(id+"F0.wireOp",EDGE,"E11.21.1"),sQuery(id+"F0.wireOp",EDGE,"E11.21.2"),sQuery(id+"F0.wireOp",EDGE,"E11.21.3"),sQuery(id+"F0.wireOp",EDGE,"E11.21.4"),sQuery(id+"F0.wireOp",EDGE,"E11.21.5"),sQuery(id+"F0.wireOp",EDGE,"E11.22.0"),sQuery(id+"F0.wireOp",EDGE,"E11.22.1"),sQuery(id+"F0.wireOp",EDGE,"E11.22.2"),sQuery(id+"F0.wireOp",EDGE,"E11.22.3"),sQuery(id+"F0.wireOp",EDGE,"E11.22.4"),sQuery(id+"F0.wireOp",EDGE,"E11.22.5"),sQuery(id+"F0.wireOp",EDGE,"E11.23.0"),sQuery(id+"F0.wireOp",EDGE,"E11.23.1"),sQuery(id+"F0.wireOp",EDGE,"E11.23.2"),sQuery(id+"F0.wireOp",EDGE,"E11.23.3"),sQuery(id+"F0.wireOp",EDGE,"E11.23.4"),sQuery(id+"F0.wireOp",EDGE,"E11.23.5"),sQuery(id+"F0.wireOp",EDGE,"E11.24.0"),sQuery(id+"F0.wireOp",EDGE,"E11.24.1"),sQuery(id+"F0.wireOp",EDGE,"E11.24.2"),sQuery(id+"F0.wireOp",EDGE,"E11.24.3"),sQuery(id+"F0.wireOp",EDGE,"E11.24.4"),sQuery(id+"F0.wireOp",EDGE,"E11.24.5"),sQuery(id+"F0.wireOp",EDGE,"E11.25.0"),sQuery(id+"F0.wireOp",EDGE,"E11.25.1"),sQuery(id+"F0.wireOp",EDGE,"E11.25.2"),sQuery(id+"F0.wireOp",EDGE,"E11.25.3"),sQuery(id+"F0.wireOp",EDGE,"E11.25.4"),sQuery(id+"F0.wireOp",EDGE,"E11.25.5"),sQuery(id+"F0.wireOp",EDGE,"E11.26.0"),sQuery(id+"F0.wireOp",EDGE,"E11.26.1"),sQuery(id+"F0.wireOp",EDGE,"E11.26.2"),sQuery(id+"F0.wireOp",EDGE,"E11.26.3"),sQuery(id+"F0.wireOp",EDGE,"E11.26.4"),sQuery(id+"F0.wireOp",EDGE,"E11.26.5"),sQuery(id+"F0.wireOp",EDGE,"E11.27.0"),sQuery(id+"F0.wireOp",EDGE,"E11.27.1"),sQuery(id+"F0.wireOp",EDGE,"E11.27.2"),sQuery(id+"F0.wireOp",EDGE,"E11.27.3"),sQuery(id+"F0.wireOp",EDGE,"E11.27.4"),sQuery(id+"F0.wireOp",EDGE,"E11.27.5"),sQuery(id+"F0.wireOp",EDGE,"E11.28.0"),sQuery(id+"F0.wireOp",EDGE,"E11.28.1"),sQuery(id+"F0.wireOp",EDGE,"E11.28.2"),sQuery(id+"F0.wireOp",EDGE,"E11.28.3"),sQuery(id+"F0.wireOp",EDGE,"E11.28.4"),sQuery(id+"F0.wireOp",EDGE,"E11.28.5"),sQuery(id+"F0.wireOp",EDGE,"E11.29.0"),sQuery(id+"F0.wireOp",EDGE,"E11.29.1"),sQuery(id+"F0.wireOp",EDGE,"E11.29.2"),sQuery(id+"F0.wireOp",EDGE,"E11.29.3"),sQuery(id+"F0.wireOp",EDGE,"E11.29.4"),sQuery(id+"F0.wireOp",EDGE,"E11.29.5"),sQuery(id+"F0.wireOp",EDGE,"E11.30.0"),sQuery(id+"F0.wireOp",EDGE,"E11.30.1"),sQuery(id+"F0.wireOp",EDGE,"E11.30.2"),sQuery(id+"F0.wireOp",EDGE,"E11.30.3"),sQuery(id+"F0.wireOp",EDGE,"E11.30.4"),sQuery(id+"F0.wireOp",EDGE,"E11.30.5"),sQuery(id+"F0.wireOp",EDGE,"E11.31.0"),sQuery(id+"F0.wireOp",EDGE,"E11.31.1"),sQuery(id+"F0.wireOp",EDGE,"E11.31.2"),sQuery(id+"F0.wireOp",EDGE,"E11.31.3"),sQuery(id+"F0.wireOp",EDGE,"E11.31.4"),sQuery(id+"F0.wireOp",EDGE,"E11.31.5"),sQuery(id+"F0.wireOp",EDGE,"E11.32.0"),sQuery(id+"F0.wireOp",EDGE,"E11.32.1"),sQuery(id+"F0.wireOp",EDGE,"E11.32.2"),sQuery(id+"F0.wireOp",EDGE,"E11.32.3"),sQuery(id+"F0.wireOp",EDGE,"E11.32.4"),sQuery(id+"F0.wireOp",EDGE,"E11.32.5"),sQuery(id+"F0.wireOp",EDGE,"E11.33.0"),sQuery(id+"F0.wireOp",EDGE,"E11.33.1"),sQuery(id+"F0.wireOp",EDGE,"E11.33.2"),sQuery(id+"F0.wireOp",EDGE,"E11.33.3"),sQuery(id+"F0.wireOp",EDGE,"E11.33.4"),sQuery(id+"F0.wireOp",EDGE,"E11.33.5"),sQuery(id+"F0.wireOp",EDGE,"E11.34.0"),sQuery(id+"F0.wireOp",EDGE,"E11.34.1"),sQuery(id+"F0.wireOp",EDGE,"E11.34.2"),sQuery(id+"F0.wireOp",EDGE,"E11.34.3"),sQuery(id+"F0.wireOp",EDGE,"E11.34.4"),sQuery(id+"F0.wireOp",EDGE,"E11.34.5"),sQuery(id+"F0.wireOp",EDGE,"E11.35.0"),sQuery(id+"F0.wireOp",EDGE,"E11.35.1"),sQuery(id+"F0.wireOp",EDGE,"E11.35.2"),sQuery(id+"F0.wireOp",EDGE,"E11.35.3"),sQuery(id+"F0.wireOp",EDGE,"E11.35.4"),sQuery(id+"F0.wireOp",EDGE,"E11.35.5"),sQuery(id+"F0.wireOp",EDGE,"E11.36.0"),sQuery(id+"F0.wireOp",EDGE,"E11.36.1"),sQuery(id+"F0.wireOp",EDGE,"E11.36.2"),sQuery(id+"F0.wireOp",EDGE,"E11.36.3"),sQuery(id+"F0.wireOp",EDGE,"E11.36.4"),sQuery(id+"F0.wireOp",EDGE,"E11.36.5"),sQuery(id+"F0.wireOp",EDGE,"E11.37.0"),sQuery(id+"F0.wireOp",EDGE,"E11.37.1"),sQuery(id+"F0.wireOp",EDGE,"E11.37.2"),sQuery(id+"F0.wireOp",EDGE,"E11.37.3"),sQuery(id+"F0.wireOp",EDGE,"E11.37.4"),sQuery(id+"F0.wireOp",EDGE,"E11.37.5"),sQuery(id+"F0.wireOp",EDGE,"E11.38.0"),sQuery(id+"F0.wireOp",EDGE,"E11.38.1"),sQuery(id+"F0.wireOp",EDGE,"E11.38.2"),sQuery(id+"F0.wireOp",EDGE,"E11.38.3"),sQuery(id+"F0.wireOp",EDGE,"E11.38.4"),sQuery(id+"F0.wireOp",EDGE,"E11.38.5"),sQuery(id+"F0.wireOp",EDGE,"E11.39.0"),sQuery(id+"F0.wireOp",EDGE,"E11.39.1"),sQuery(id+"F0.wireOp",EDGE,"E11.39.2"),sQuery(id+"F0.wireOp",EDGE,"E11.39.3"),sQuery(id+"F0.wireOp",EDGE,"E11.39.4"),sQuery(id+"F0.wireOp",EDGE,"E11.39.5"),sQuery(id+"F0.wireOp",EDGE,"E11.40.0"),sQuery(id+"F0.wireOp",EDGE,"E11.40.1"),sQuery(id+"F0.wireOp",EDGE,"E11.40.2"),sQuery(id+"F0.wireOp",EDGE,"E11.40.3"),sQuery(id+"F0.wireOp",EDGE,"E11.40.4"),sQuery(id+"F0.wireOp",EDGE,"E11.40.5"),sQuery(id+"F0.wireOp",EDGE,"E11.41.0"),sQuery(id+"F0.wireOp",EDGE,"E11.41.1"),sQuery(id+"F0.wireOp",EDGE,"E11.41.2"),sQuery(id+"F0.wireOp",EDGE,"E11.41.3"),sQuery(id+"F0.wireOp",EDGE,"E11.41.4"),sQuery(id+"F0.wireOp",EDGE,"E11.41.5"),sQuery(id+"F0.wireOp",EDGE,"E11.42.0"),sQuery(id+"F0.wireOp",EDGE,"E11.42.1"),sQuery(id+"F0.wireOp",EDGE,"E11.42.2"),sQuery(id+"F0.wireOp",EDGE,"E11.42.3"),sQuery(id+"F0.wireOp",EDGE,"E11.42.4"),sQuery(id+"F0.wireOp",EDGE,"E11.42.5"),sQuery(id+"F0.wireOp",EDGE,"E11.43.0"),sQuery(id+"F0.wireOp",EDGE,"E11.43.1"),sQuery(id+"F0.wireOp",EDGE,"E11.43.2"),sQuery(id+"F0.wireOp",EDGE,"E11.43.3"),sQuery(id+"F0.wireOp",EDGE,"E11.43.4"),sQuery(id+"F0.wireOp",EDGE,"E11.43.5"),sQuery(id+"F0.wireOp",EDGE,"E11.44.0"),sQuery(id+"F0.wireOp",EDGE,"E11.44.1"),sQuery(id+"F0.wireOp",EDGE,"E11.44.2"),sQuery(id+"F0.wireOp",EDGE,"E11.44.3"),sQuery(id+"F0.wireOp",EDGE,"E11.44.4"),sQuery(id+"F0.wireOp",EDGE,"E11.44.5"),sQuery(id+"F0.wireOp",EDGE,"E11.45.0"),sQuery(id+"F0.wireOp",EDGE,"E11.45.1"),sQuery(id+"F0.wireOp",EDGE,"E11.45.2"),sQuery(id+"F0.wireOp",EDGE,"E11.45.3"),sQuery(id+"F0.wireOp",EDGE,"E11.45.4"),sQuery(id+"F0.wireOp",EDGE,"E11.45.5"),sQuery(id+"F0.wireOp",EDGE,"E11.46.0"),sQuery(id+"F0.wireOp",EDGE,"E11.46.1"),sQuery(id+"F0.wireOp",EDGE,"E11.46.2"),sQuery(id+"F0.wireOp",EDGE,"E11.46.3"),sQuery(id+"F0.wireOp",EDGE,"E11.46.4"),sQuery(id+"F0.wireOp",EDGE,"E11.46.5"),sQuery(id+"F0.wireOp",EDGE,"E11.47.0"),sQuery(id+"F0.wireOp",EDGE,"E11.47.1"),sQuery(id+"F0.wireOp",EDGE,"E11.47.2"),sQuery(id+"F0.wireOp",EDGE,"E11.47.3"),sQuery(id+"F0.wireOp",EDGE,"E11.47.4"),sQuery(id+"F0.wireOp",EDGE,"E11.47.5"),sQuery(id+"F0.wireOp",EDGE,"E11.48.0"),sQuery(id+"F0.wireOp",EDGE,"E11.48.1"),sQuery(id+"F0.wireOp",EDGE,"E11.48.2"),sQuery(id+"F0.wireOp",EDGE,"E11.48.3"),sQuery(id+"F0.wireOp",EDGE,"E11.48.4"),sQuery(id+"F0.wireOp",EDGE,"E11.48.5"),sQuery(id+"F0.wireOp",EDGE,"E11.49.0"),sQuery(id+"F0.wireOp",EDGE,"E11.49.1"),sQuery(id+"F0.wireOp",EDGE,"E11.49.2"),sQuery(id+"F0.wireOp",EDGE,"E11.49.3"),sQuery(id+"F0.wireOp",EDGE,"E11.49.4"),sQuery(id+"F0.wireOp",EDGE,"E11.49.5"),sQuery(id+"F0.wireOp",EDGE,"E11.50.0"),sQuery(id+"F0.wireOp",EDGE,"E11.50.1"),sQuery(id+"F0.wireOp",EDGE,"E11.50.2"),sQuery(id+"F0.wireOp",EDGE,"E11.50.3"),sQuery(id+"F0.wireOp",EDGE,"E11.50.4"),sQuery(id+"F0.wireOp",EDGE,"E11.50.5"),sQuery(id+"F0.wireOp",EDGE,"E11.51.0"),sQuery(id+"F0.wireOp",EDGE,"E11.51.1"),sQuery(id+"F0.wireOp",EDGE,"E11.51.2"),sQuery(id+"F0.wireOp",EDGE,"E11.51.3"),sQuery(id+"F0.wireOp",EDGE,"E11.51.4"),sQuery(id+"F0.wireOp",EDGE,"E11.51.5"),sQuery(id+"F0.wireOp",EDGE,"E11.52.0"),sQuery(id+"F0.wireOp",EDGE,"E11.52.1"),sQuery(id+"F0.wireOp",EDGE,"E11.52.2"),sQuery(id+"F0.wireOp",EDGE,"E11.52.3"),sQuery(id+"F0.wireOp",EDGE,"E11.52.4"),sQuery(id+"F0.wireOp",EDGE,"E11.52.5"),sQuery(id+"F0.wireOp",EDGE,"E11.53.0"),sQuery(id+"F0.wireOp",EDGE,"E11.53.1"),sQuery(id+"F0.wireOp",EDGE,"E11.53.2"),sQuery(id+"F0.wireOp",EDGE,"E11.53.3"),sQuery(id+"F0.wireOp",EDGE,"E11.53.4"),sQuery(id+"F0.wireOp",EDGE,"E11.53.5"),sQuery(id+"F0.wireOp",EDGE,"E11.54.0"),sQuery(id+"F0.wireOp",EDGE,"E11.54.1"),sQuery(id+"F0.wireOp",EDGE,"E11.54.2"),sQuery(id+"F0.wireOp",EDGE,"E11.54.3"),sQuery(id+"F0.wireOp",EDGE,"E11.54.4"),sQuery(id+"F0.wireOp",EDGE,"E11.54.5"),sQuery(id+"F0.wireOp",EDGE,"E11.55.0"),sQuery(id+"F0.wireOp",EDGE,"E11.55.1"),sQuery(id+"F0.wireOp",EDGE,"E11.55.2"),sQuery(id+"F0.wireOp",EDGE,"E11.55.3"),sQuery(id+"F0.wireOp",EDGE,"E11.55.4"),sQuery(id+"F0.wireOp",EDGE,"E11.55.5"),sQuery(id+"F0.wireOp",EDGE,"E11.56.0"),sQuery(id+"F0.wireOp",EDGE,"E11.56.1"),sQuery(id+"F0.wireOp",EDGE,"E11.56.2"),sQuery(id+"F0.wireOp",EDGE,"E11.56.3"),sQuery(id+"F0.wireOp",EDGE,"E11.56.4"),sQuery(id+"F0.wireOp",EDGE,"E11.56.5"),sQuery(id+"F0.wireOp",EDGE,"E11.57.0"),sQuery(id+"F0.wireOp",EDGE,"E11.57.1"),sQuery(id+"F0.wireOp",EDGE,"E11.57.2"),sQuery(id+"F0.wireOp",EDGE,"E11.57.3"),sQuery(id+"F0.wireOp",EDGE,"E11.57.4"),sQuery(id+"F0.wireOp",EDGE,"E11.57.5"),sQuery(id+"F0.wireOp",EDGE,"E11.58.0"),sQuery(id+"F0.wireOp",EDGE,"E11.58.1"),sQuery(id+"F0.wireOp",EDGE,"E11.58.2"),sQuery(id+"F0.wireOp",EDGE,"E11.58.3"),sQuery(id+"F0.wireOp",EDGE,"E11.58.4"),sQuery(id+"F0.wireOp",EDGE,"E11.58.5"),sQuery(id+"F0.wireOp",EDGE,"E11.59.0"),sQuery(id+"F0.wireOp",EDGE,"E11.59.1"),sQuery(id+"F0.wireOp",EDGE,"E11.59.2"),sQuery(id+"F0.wireOp",EDGE,"E11.59.3"),sQuery(id+"F0.wireOp",EDGE,"E11.59.4"),sQuery(id+"F0.wireOp",EDGE,"E11.59.5")])],"isStart":false});
            var sketch = newSketch(context, id + "F2", { "sketchPlane" : qUnion([Q0])});
            skCircle(sketch, "E12", {"center": v(0, 0) * mm, "radius": 11.43 * mm});
            skSolve(sketch);
        }
        {
            var Q0;
            Q0=makeQuery(id+"F2.imprint","IMPRINT",FACE,{"disambiguationData":[TD([[makeQuery(id+"F2.imprint","IMPRINT",EDGE,{"derivedFrom":sQuery(id+"F2.wireOp",EDGE,"E12")}),1.0]])]});
            extrude(context, id + "F3", {"entities" : qUnion([Q0]), "operationType" : NewBodyOperationType.ADD, "depth" : 7.37 * mm});
        }
        {
            var Q0;
            Q0=makeQuery(id+"F3.opExtrude","CAP_FACE",FACE,{"disambiguationData":[OSD([sQuery(id+"F2.wireOp",EDGE,"E12")])],"isStart":false});
            var sketch = newSketch(context, id + "F4", { "sketchPlane" : qUnion([Q0])});
            skCircle(sketch, "E13.cCircle", {"center": v(0, 0) * mm, "radius": 5.56 * mm, "construction": true});
            skLineSegment(sketch, "E13.0", {"start": v(6.42, 0.03) * mm, "end": v(3.24, -5.55) * mm});
            skLineSegment(sketch, "E13.1", {"start": v(3.24, -5.55) * mm, "end": v(-3.18, -5.58) * mm});
            skLineSegment(sketch, "E13.2", {"start": v(-3.18, -5.58) * mm, "end": v(-6.42, -0.03) * mm});
            skLineSegment(sketch, "E13.3", {"start": v(-6.42, -0.03) * mm, "end": v(-3.24, 5.55) * mm});
            skLineSegment(sketch, "E13.4", {"start": v(-3.24, 5.55) * mm, "end": v(3.18, 5.58) * mm});
            skLineSegment(sketch, "E13.5", {"start": v(3.18, 5.58) * mm, "end": v(6.42, 0.03) * mm});
            skPoint(sketch, "E13.0.midPoint", {"position": v(4.83, -2.76) * mm});
            skSolve(sketch);
        }
        {
            var Q0;
            Q0=makeQuery(id+"F4.imprint","IMPRINT",FACE,{"disambiguationData":[TD([[makeQuery(id+"F4.imprint","IMPRINT",EDGE,{"derivedFrom":sQuery(id+"F4.wireOp",EDGE,"E13.0")}),-1.0]])]});
            extrude(context, id + "F5", {"entities" : qUnion([Q0]), "operationType" : NewBodyOperationType.REMOVE, "oppositeDirection" : true, "depth" : 25.4 * mm});
        }
    });
